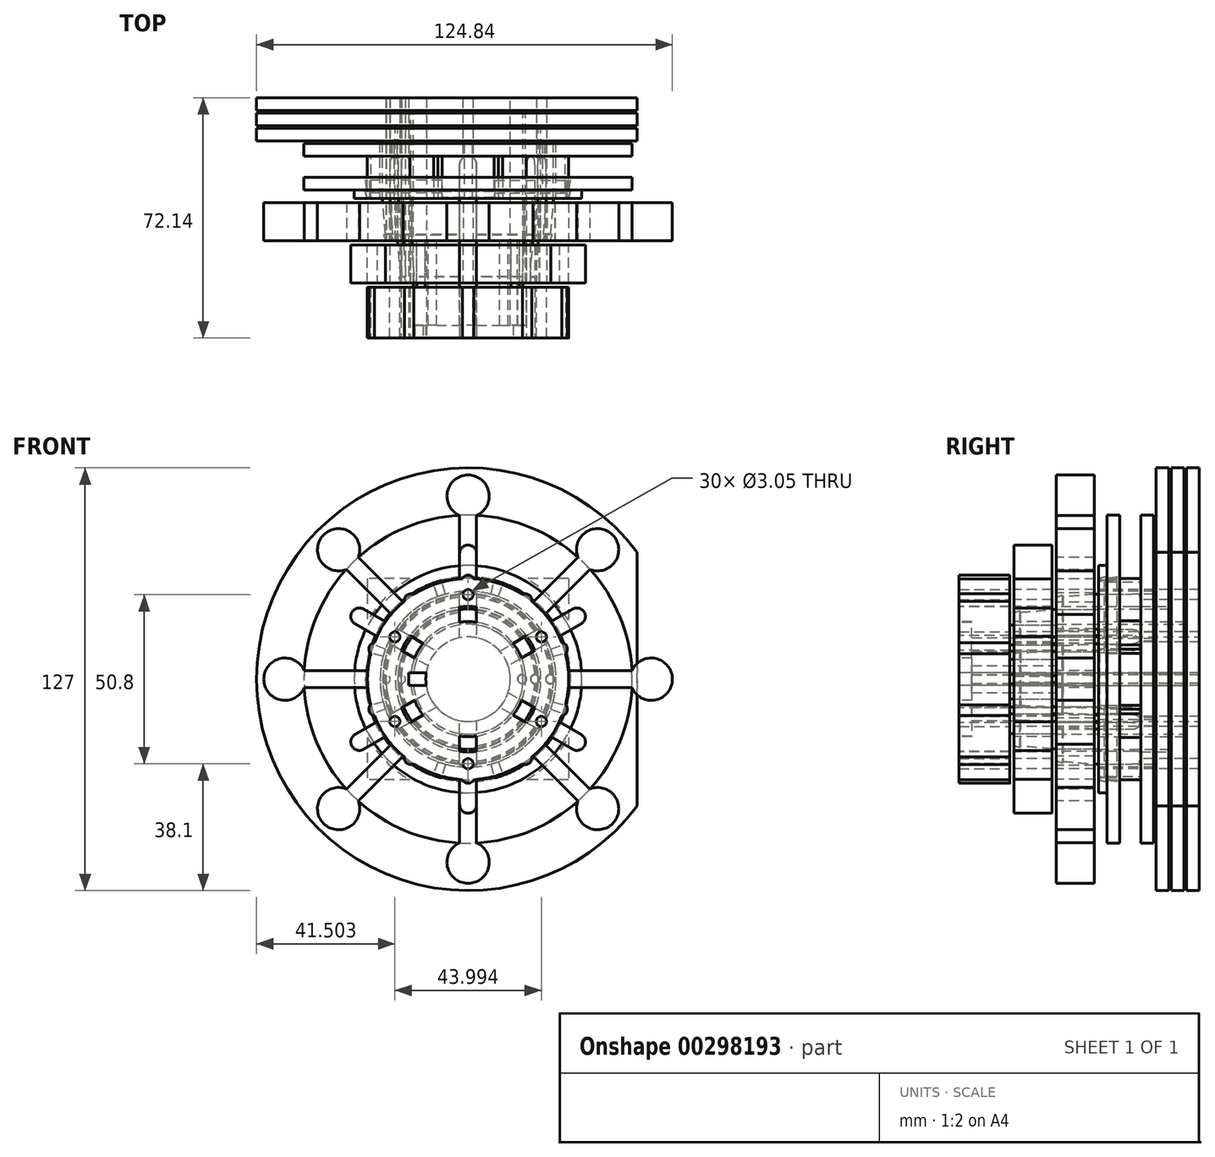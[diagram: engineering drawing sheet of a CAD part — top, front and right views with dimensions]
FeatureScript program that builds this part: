
annotation { "Feature Type Name" : "Feature", "Feature Type Description" : "" }
export const myFeature = defineFeature(function(context is Context, id is Id, definition is map)
    precondition{}
    {
        {
            var Q0;
            Q0=qCreatedBy(makeId("Top.planeOp"),FACE);
            var sketch = newSketch(context, id + "F0", { "sketchPlane" : qUnion([Q0])});
            skLineSegment(sketch, "E0", {"start": v(0, 0) * mm, "end": v(0, -79.23) * mm, "construction": true});
            skLineSegment(sketch, "E1", {"start": v(63.5, 0) * mm, "end": v(12.7, 0) * mm});
            skLineSegment(sketch, "E2", {"start": v(12.7, 0) * mm, "end": v(12.7, -68.33) * mm});
            skLineSegment(sketch, "E3", {"start": v(12.7, -68.33) * mm, "end": v(16.51, -68.33) * mm});
            skLineSegment(sketch, "E4", {"start": v(16.51, -68.33) * mm, "end": v(16.5, -3.81) * mm});
            skLineSegment(sketch, "E5", {"start": v(16.5, -3.81) * mm, "end": v(63.5, -3.8) * mm});
            skLineSegment(sketch, "E6", {"start": v(63.5, -3.8) * mm, "end": v(63.5, 0) * mm});
            skLineSegment(sketch, "E7", {"start": v(63.5, -4.57) * mm, "end": v(17.27, -4.57) * mm});
            skLineSegment(sketch, "E8", {"start": v(17.27, -4.57) * mm, "end": v(17.27, -55.63) * mm});
            skLineSegment(sketch, "E9", {"start": v(17.27, -55.63) * mm, "end": v(21.08, -55.63) * mm});
            skLineSegment(sketch, "E10", {"start": v(21.08, -55.63) * mm, "end": v(21.08, -8.38) * mm});
            skLineSegment(sketch, "E11", {"start": v(21.08, -8.38) * mm, "end": v(63.5, -8.38) * mm});
            skLineSegment(sketch, "E12", {"start": v(63.5, -8.38) * mm, "end": v(63.5, -4.57) * mm});
            skLineSegment(sketch, "E13", {"start": v(63.5, -9.14) * mm, "end": v(21.84, -9.14) * mm});
            skLineSegment(sketch, "E14", {"start": v(21.84, -9.14) * mm, "end": v(21.84, -42.93) * mm});
            skLineSegment(sketch, "E15", {"start": v(21.84, -42.93) * mm, "end": v(25.65, -42.93) * mm});
            skLineSegment(sketch, "E16", {"start": v(25.65, -42.93) * mm, "end": v(25.65, -12.95) * mm});
            skLineSegment(sketch, "E17", {"start": v(25.65, -12.95) * mm, "end": v(63.5, -12.95) * mm});
            skLineSegment(sketch, "E18", {"start": v(63.5, -12.95) * mm, "end": v(63.5, -9.14) * mm});
            skLineSegment(sketch, "E19", {"start": v(49.28, -13.72) * mm, "end": v(26.42, -13.72) * mm});
            skLineSegment(sketch, "E20", {"start": v(26.42, -13.72) * mm, "end": v(26.42, -30.23) * mm});
            skLineSegment(sketch, "E21", {"start": v(26.42, -30.23) * mm, "end": v(30.23, -30.23) * mm});
            skLineSegment(sketch, "E22", {"start": v(30.23, -30.23) * mm, "end": v(30.23, -17.53) * mm});
            skLineSegment(sketch, "E23", {"start": v(30.23, -17.53) * mm, "end": v(49.28, -17.53) * mm});
            skLineSegment(sketch, "E24", {"start": v(49.28, -17.53) * mm, "end": v(49.28, -13.72) * mm});
            skLineSegment(sketch, "E25", {"start": v(49.28, -23.88) * mm, "end": v(30.35, -23.88) * mm});
            skLineSegment(sketch, "E26", {"start": v(30.35, -23.88) * mm, "end": v(30.35, -27.57) * mm});
            skLineSegment(sketch, "E27", {"start": v(30.35, -30.23) * mm, "end": v(34.16, -30.23) * mm});
            skLineSegment(sketch, "E28", {"start": v(34.16, -30.23) * mm, "end": v(34.16, -27.69) * mm});
            skLineSegment(sketch, "E29", {"start": v(34.16, -27.69) * mm, "end": v(49.28, -27.69) * mm});
            skLineSegment(sketch, "E30", {"start": v(49.28, -27.69) * mm, "end": v(49.28, -23.88) * mm});
            skLineSegment(sketch, "E31", {"start": v(25.65, -31.5) * mm, "end": v(24.82, -41.03) * mm});
            skLineSegment(sketch, "E32", {"start": v(21.08, -44.2) * mm, "end": v(20.08, -55.63) * mm});
            skLineSegment(sketch, "E33", {"start": v(16.51, -56.9) * mm, "end": v(15.51, -68.33) * mm});
            skLineSegment(sketch, "E34", {"start": v(25.65, -31.5) * mm, "end": v(30.23, -31.5) * mm});
            skLineSegment(sketch, "E35", {"start": v(30.23, -31.5) * mm, "end": v(30.23, -42.93) * mm});
            skLineSegment(sketch, "E36", {"start": v(30.23, -42.93) * mm, "end": v(25.65, -42.93) * mm});
            skLineSegment(sketch, "E37", {"start": v(21.08, -44.2) * mm, "end": v(30.23, -44.2) * mm});
            skLineSegment(sketch, "E38", {"start": v(30.23, -44.2) * mm, "end": v(30.23, -55.63) * mm});
            skLineSegment(sketch, "E39", {"start": v(30.23, -55.63) * mm, "end": v(21.08, -55.63) * mm});
            skLineSegment(sketch, "E40", {"start": v(16.51, -56.9) * mm, "end": v(30.23, -56.9) * mm});
            skLineSegment(sketch, "E41", {"start": v(30.23, -56.9) * mm, "end": v(30.23, -68.33) * mm});
            skLineSegment(sketch, "E42", {"start": v(30.23, -68.33) * mm, "end": v(16.51, -68.33) * mm});
            skLineSegment(sketch, "E43", {"start": v(25.33, -41.08) * mm, "end": v(24.65, -42.93) * mm});
            skLineSegment(sketch, "E44", {"start": v(25.33, -41.08) * mm, "end": v(24.83, -40.9) * mm});
            skLineSegment(sketch, "E45", {"start": v(25.28, -41.2) * mm, "end": v(24.82, -41.03) * mm});
            skLineSegment(sketch, "E46", {"start": v(30.35, -29.97) * mm, "end": v(30.86, -28.08) * mm});
            skLineSegment(sketch, "E47", {"start": v(30.86, -28.08) * mm, "end": v(30.35, -27.57) * mm});
            skLineSegment(sketch, "E48", {"start": v(30.23, -29.97) * mm, "end": v(30.73, -28.08) * mm});
            skLineSegment(sketch, "E49", {"start": v(30.73, -28.08) * mm, "end": v(30.23, -27.57) * mm});
            skLineSegment(sketch, "E50.trimOffspring", {"start": v(30.35, -29.97) * mm, "end": v(30.35, -30.23) * mm});
            skLineSegment(sketch, "E51", {"start": v(30.35, -27.57) * mm, "end": v(30.86, -23.88) * mm});
            skLineSegment(sketch, "E52", {"start": v(20.08, -55.63) * mm, "end": v(20.73, -53.84) * mm});
            skLineSegment(sketch, "E53", {"start": v(20.73, -53.84) * mm, "end": v(20.25, -53.67) * mm});
            skLineSegment(sketch, "E54", {"start": v(15.51, -68.33) * mm, "end": v(16.16, -66.54) * mm});
            skLineSegment(sketch, "E55", {"start": v(16.16, -66.54) * mm, "end": v(15.68, -66.37) * mm});
            skSolve(sketch);
        }
        {
            var Q0;
            Q0=makeQuery(id+"F0.imprint","IMPRINT",FACE,{"disambiguationData":[TD([[makeQuery(id+"F0.imprint","IMPRINT",EDGE,{"derivedFrom":sQuery(id+"F0.wireOp",EDGE,"E1")}),1.0]])]});
            var Q1;
            Q1=sQuery(id+"F0.wireOp",EDGE,"E0");
            revolve(context, id + "F1", {"entities" : qUnion([Q0]), "axis" : qUnion([Q1]), "revolveType" : RevolveType.FULL});
        }
        {
            var Q0;
            Q0=makeQuery(id+"F0.imprint","IMPRINT",FACE,{"disambiguationData":[TD([[makeQuery(id+"F0.imprint","IMPRINT",EDGE,{"derivedFrom":sQuery(id+"F0.wireOp",EDGE,"E7")}),1.0]])]});
            var Q1;
            {var subQ0=sQuery(id+"F0.wireOp",EDGE,"E52");Q1=makeQuery(id+"F0.imprint","IMPRINT",FACE,{"disambiguationData":[TD([[makeQuery(id+"F0.imprint","IMPRINT",EDGE,{"derivedFrom":subQ0}),1.0]])]});}
            var Q2;
            Q2=sQuery(id+"F0.wireOp",EDGE,"E0");
            revolve(context, id + "F2", {"surfaceOperationType" : NewSurfaceOperationType.NEW, "entities" : qUnion([Q0, Q1]), "axis" : qUnion([Q2]), "revolveType" : RevolveType.FULL});
        }
        {
            var Q0;
            Q0=makeQuery(id+"F0.imprint","IMPRINT",FACE,{"disambiguationData":[TD([[makeQuery(id+"F0.imprint","IMPRINT",EDGE,{"derivedFrom":sQuery(id+"F0.wireOp",EDGE,"E13")}),1.0]])]});
            var Q1;
            Q1=sQuery(id+"F0.wireOp",EDGE,"E0");
            revolve(context, id + "F3", {"entities" : qUnion([Q0]), "axis" : qUnion([Q1]), "revolveType" : RevolveType.FULL});
        }
        {
            var Q0;
            Q0=makeQuery(id+"F0.imprint","IMPRINT",FACE,{"disambiguationData":[TD([[makeQuery(id+"F0.imprint","IMPRINT",EDGE,{"derivedFrom":sQuery(id+"F0.wireOp",EDGE,"E19")}),1.0]])]});
            var Q1;
            {var subQ0=sQuery(id+"F0.wireOp",EDGE,"E48");Q1=makeQuery(id+"F0.imprint","IMPRINT",FACE,{"disambiguationData":[TD([[makeQuery(id+"F0.imprint","IMPRINT",EDGE,{"derivedFrom":subQ0}),1.0]])]});}
            var Q2;
            {var subQ0=sQuery(id+"F0.wireOp",EDGE,"E54");Q2=makeQuery(id+"F0.imprint","IMPRINT",FACE,{"disambiguationData":[TD([[makeQuery(id+"F0.imprint","IMPRINT",EDGE,{"derivedFrom":subQ0}),1.0]])]});}
            var Q3;
            Q3=sQuery(id+"F0.wireOp",EDGE,"E0");
            revolve(context, id + "F4", {"operationType" : NewBodyOperationType.ADD, "surfaceOperationType" : NewSurfaceOperationType.NEW, "entities" : qUnion([Q0, Q1, Q2]), "axis" : qUnion([Q3]), "revolveType" : RevolveType.FULL});
        }
        {
            var Q0;
            Q0=makeQuery(id+"F0.imprint","IMPRINT",FACE,{"disambiguationData":[TD([[makeQuery(id+"F0.imprint","IMPRINT",EDGE,{"derivedFrom":sQuery(id+"F0.wireOp",EDGE,"E27")}),1.0]])]});
            var Q1;
            Q1=sQuery(id+"F0.wireOp",EDGE,"E0");
            revolve(context, id + "F5", {"surfaceOperationType" : NewSurfaceOperationType.NEW, "entities" : qUnion([Q0]), "axis" : qUnion([Q1]), "revolveType" : RevolveType.FULL});
        }
        {
            var Q0;
            Q0=qCreatedBy(makeId("Front.planeOp"),FACE);
            var sketch = newSketch(context, id + "F6", { "sketchPlane" : qUnion([Q0])});
            skCircle(sketch, "E56.0", {"center": v(0, 0) * mm, "radius": 63.5 * mm});
            skLineSegment(sketch, "E57", {"start": v(50.8, 38.1) * mm, "end": v(50.8, -38.1) * mm});
            skSolve(sketch);
        }
        {
            var Q0;
            {var subQ0=sQuery(id+"F6.wireOp",EDGE,"E57");Q0=makeQuery(id+"F6.imprint","IMPRINT",FACE,{"disambiguationData":[TD([[makeQuery(id+"F6.imprint","IMPRINT",EDGE,{"derivedFrom":subQ0}),1.0]])]});}
            extrude(context, id + "F7", {"entities" : qUnion([Q0]), "operationType" : NewBodyOperationType.REMOVE, "endBound" : BoundingType.THROUGH_ALL, "depth" : 25.4 * mm});
        }
        {
            var Q0;
            {var subQ2=sQuery(id+"F0.wireOp",EDGE,"E34");Q0=makeQuery(id+"F0.imprint","IMPRINT",FACE,{"disambiguationData":[TD([[makeQuery(id+"F0.imprint","IMPRINT",EDGE,{"derivedFrom":subQ2}),-1.0]])]});}
            var Q1;
            {var subQ0=sQuery(id+"F0.wireOp",EDGE,"E44");Q1=makeQuery(id+"F0.imprint","IMPRINT",FACE,{"disambiguationData":[TD([[makeQuery(id+"F0.imprint","IMPRINT",EDGE,{"derivedFrom":subQ0}),-1.0]])]});}
            var Q2;
            Q2=sQuery(id+"F0.wireOp",EDGE,"E0");
            revolve(context, id + "F8", {"entities" : qUnion([Q0, Q1]), "axis" : qUnion([Q2]), "revolveType" : RevolveType.FULL});
        }
        {
            var Q0;
            {var subQ2=sQuery(id+"F0.wireOp",EDGE,"E37");Q0=makeQuery(id+"F0.imprint","IMPRINT",FACE,{"disambiguationData":[TD([[makeQuery(id+"F0.imprint","IMPRINT",EDGE,{"derivedFrom":subQ2}),-1.0]])]});}
            var Q1;
            {var subQ0=sQuery(id+"F0.wireOp",EDGE,"E52");Q1=makeQuery(id+"F0.imprint","IMPRINT",FACE,{"disambiguationData":[TD([[makeQuery(id+"F0.imprint","IMPRINT",EDGE,{"derivedFrom":subQ0}),-1.0]])]});}
            var Q2;
            Q2=sQuery(id+"F0.wireOp",EDGE,"E0");
            revolve(context, id + "F9", {"surfaceOperationType" : NewSurfaceOperationType.NEW, "entities" : qUnion([Q0, Q1]), "axis" : qUnion([Q2]), "revolveType" : RevolveType.FULL});
        }
        {
            var Q0;
            {var subQ2=sQuery(id+"F0.wireOp",EDGE,"E40");Q0=makeQuery(id+"F0.imprint","IMPRINT",FACE,{"disambiguationData":[TD([[makeQuery(id+"F0.imprint","IMPRINT",EDGE,{"derivedFrom":subQ2}),-1.0]])]});}
            var Q1;
            {var subQ0=sQuery(id+"F0.wireOp",EDGE,"E54");Q1=makeQuery(id+"F0.imprint","IMPRINT",FACE,{"disambiguationData":[TD([[makeQuery(id+"F0.imprint","IMPRINT",EDGE,{"derivedFrom":subQ0}),-1.0]])]});}
            var Q2;
            Q2=sQuery(id+"F0.wireOp",EDGE,"E0");
            revolve(context, id + "F10", {"surfaceOperationType" : NewSurfaceOperationType.NEW, "entities" : qUnion([Q0, Q1]), "axis" : qUnion([Q2]), "revolveType" : RevolveType.FULL});
        }
        {
            var Q0;
            Q0=makeQuery(id+"F10.opRevolve","SWEPT_FACE",FACE,{"disambiguationData":[OSD([sQuery(id+"F0.wireOp",EDGE,"E3"),sQuery(id+"F0.wireOp",EDGE,"E42")])]});
            var sketch = newSketch(context, id + "F11", { "sketchPlane" : qUnion([Q0])});
            skCircle(sketch, "E58.0", {"center": v(0, 0) * mm, "radius": 30.23 * mm});
            skCircle(sketch, "E59", {"center": v(0, 25.4) * mm, "radius": 1.52 * mm});
            skCircle(sketch, "E60.1.0", {"center": v(-22, 12.7) * mm, "radius": 1.52 * mm});
            skCircle(sketch, "E60.2.0", {"center": v(-22, -12.7) * mm, "radius": 1.52 * mm});
            skCircle(sketch, "E60.3.0", {"center": v(0, -25.4) * mm, "radius": 1.52 * mm});
            skCircle(sketch, "E60.4.0", {"center": v(22, -12.7) * mm, "radius": 1.52 * mm});
            skCircle(sketch, "E60.5.0", {"center": v(22, 12.7) * mm, "radius": 1.52 * mm});
            skSolve(sketch);
        }
        {
            var Q0;
            Q0 = qSketchRegion(id + "F11", true);
            extrude(context, id + "F12", {"entities" : qUnion([Q0]), "operationType" : NewBodyOperationType.ADD, "offsetDistance" : 25.4 * mm, "depth" : 3.8 * mm});
        }
        {
            var Q0;
            Q0=makeQuery(id+"F4.opRevolve","SWEPT_FACE",FACE,{"disambiguationData":[OSD([sQuery(id+"F0.wireOp",EDGE,"E23")])]});
            var sketch = newSketch(context, id + "F13", { "sketchPlane" : qUnion([Q0])});
            skCircle(sketch, "E61.0", {"center": v(0, 0) * mm, "radius": 30.23 * mm});
            skLineSegment(sketch, "E62.bottom", {"start": v(30.23, 30.23) * mm, "end": v(-30.23, 30.23) * mm});
            skLineSegment(sketch, "E62.top", {"start": v(30.23, -30.23) * mm, "end": v(-30.23, -30.23) * mm});
            skLineSegment(sketch, "E62.left", {"start": v(30.23, 30.23) * mm, "end": v(30.23, -30.23) * mm});
            skLineSegment(sketch, "E62.right", {"start": v(-30.23, 30.23) * mm, "end": v(-30.23, -30.23) * mm});
            skCircle(sketch, "E63", {"center": v(0, 0) * mm, "radius": 34.93 * mm});
            skSolve(sketch);
        }
        {
            var Q0;
            Q0=makeQuery(id+"F4.opRevolve","SWEPT_FACE",FACE,{"disambiguationData":[OSD([sQuery(id+"F0.wireOp",EDGE,"E21")])]});
            var sketch = newSketch(context, id + "F14", { "sketchPlane" : qUnion([Q0])});
            skLineSegment(sketch, "E64", {"start": v(0, 0) * mm, "end": v(0, 50.7) * mm, "construction": true});
            skLineSegment(sketch, "E65", {"start": v(0, 0) * mm, "end": v(55.85, 0) * mm, "construction": true});
            skCircle(sketch, "E66", {"center": v(0, 0) * mm, "radius": 30.73 * mm});
            skLineSegment(sketch, "E67", {"start": v(0, 0) * mm, "end": v(-7.95, 29.69) * mm});
            skLineSegment(sketch, "E68.MirrorCS", {"start": v(0, 0) * mm, "end": v(7.95, 29.69) * mm});
            skLineSegment(sketch, "E69", {"start": v(0, 0) * mm, "end": v(29.69, 7.95) * mm});
            skLineSegment(sketch, "E70.MirrorCS", {"start": v(0, 0) * mm, "end": v(29.69, -7.95) * mm});
            skLineSegment(sketch, "E71.MirrorCS", {"start": v(0, 0) * mm, "end": v(-29.69, 7.95) * mm});
            skLineSegment(sketch, "E72.MirrorCS", {"start": v(0, 0) * mm, "end": v(-29.69, -7.95) * mm});
            skLineSegment(sketch, "E73.MirrorCS", {"start": v(0, 0) * mm, "end": v(7.95, -29.69) * mm});
            skLineSegment(sketch, "E74.MirrorCS", {"start": v(0, 0) * mm, "end": v(-7.95, -29.69) * mm});
            skLineSegment(sketch, "E75", {"start": v(0, 0) * mm, "end": v(-10.51, 28.88) * mm});
            skLineSegment(sketch, "E76.MirrorCS", {"start": v(0, 0) * mm, "end": v(10.51, 28.88) * mm});
            skLineSegment(sketch, "E77.MirrorCS", {"start": v(0, 0) * mm, "end": v(10.51, -28.88) * mm});
            skLineSegment(sketch, "E78.MirrorCS", {"start": v(0, 0) * mm, "end": v(-10.51, -28.88) * mm});
            skLineSegment(sketch, "E79", {"start": v(0, 0) * mm, "end": v(28.88, 10.51) * mm});
            skLineSegment(sketch, "E80.MirrorCS", {"start": v(0, 0) * mm, "end": v(28.88, -10.51) * mm});
            skLineSegment(sketch, "E81.MirrorCS", {"start": v(0, 0) * mm, "end": v(-28.88, 10.51) * mm});
            skLineSegment(sketch, "E82.MirrorCS", {"start": v(0, 0) * mm, "end": v(-28.88, -10.51) * mm});
            skSolve(sketch);
        }
        {
            var Q0;
            {var subQ0=sQuery(id+"F13.wireOp",EDGE,"E62.right");var subQ1=sQuery(id+"F13.wireOp",EDGE,"E62.bottom");var subQ2=makeQuery(id+"F13.imprint","INTERSECT",VERTEX,{"derivedFrom":[subQ1,subQ0]});Q0=makeQuery(id+"F13.imprint","IMPRINT",FACE,{"disambiguationData":[TD([[makeQuery(id+"F13.imprint","IMPRINT",EDGE,{"disambiguationData":[TD([[subQ2,1.0]])],"derivedFrom":subQ1}),1.0]])]});}
            var Q1;
            {var subQ0=sQuery(id+"F13.wireOp",EDGE,"E62.left");var subQ1=sQuery(id+"F13.wireOp",EDGE,"E62.bottom");var subQ2=makeQuery(id+"F13.imprint","INTERSECT",VERTEX,{"derivedFrom":[subQ1,subQ0]});Q1=makeQuery(id+"F13.imprint","IMPRINT",FACE,{"disambiguationData":[TD([[makeQuery(id+"F13.imprint","IMPRINT",EDGE,{"disambiguationData":[TD([[subQ2,-1.0]])],"derivedFrom":subQ1}),1.0]])]});}
            var Q2;
            {var subQ0=sQuery(id+"F13.wireOp",EDGE,"E62.left");var subQ1=sQuery(id+"F13.wireOp",EDGE,"E62.top");var subQ2=makeQuery(id+"F13.imprint","INTERSECT",VERTEX,{"derivedFrom":[subQ1,subQ0]});Q2=makeQuery(id+"F13.imprint","IMPRINT",FACE,{"disambiguationData":[TD([[makeQuery(id+"F13.imprint","IMPRINT",EDGE,{"disambiguationData":[TD([[subQ2,-1.0]])],"derivedFrom":subQ1}),-1.0]])]});}
            var Q3;
            {var subQ0=sQuery(id+"F13.wireOp",EDGE,"E62.right");var subQ1=sQuery(id+"F13.wireOp",EDGE,"E62.top");var subQ2=makeQuery(id+"F13.imprint","INTERSECT",VERTEX,{"derivedFrom":[subQ1,subQ0]});Q3=makeQuery(id+"F13.imprint","IMPRINT",FACE,{"disambiguationData":[TD([[makeQuery(id+"F13.imprint","IMPRINT",EDGE,{"disambiguationData":[TD([[subQ2,1.0]])],"derivedFrom":subQ1}),-1.0]])]});}
            var Q4;
            Q4=makeQuery(id+"F4.opRevolve","SWEPT_FACE",FACE,{"disambiguationData":[OSD([sQuery(id+"F0.wireOp",EDGE,"E21")])]});
            extrude(context, id + "F15", {"entities" : qUnion([Q0, Q1, Q2, Q3]), "operationType" : NewBodyOperationType.ADD, "endBoundEntityFace" : qUnion([Q4]), "offsetDistance" : 25.4 * mm, "depth" : 6.35 * mm});
        }
        {
            var Q0;
            Q0=makeQuery(id+"F3.opRevolve","SWEPT_FACE",FACE,{"disambiguationData":[OSD([sQuery(id+"F0.wireOp",EDGE,"E15")])]});
            var sketch = newSketch(context, id + "F16", { "sketchPlane" : qUnion([Q0])});
            skCircle(sketch, "E83", {"center": v(24.65, 0) * mm, "radius": 1.27 * mm});
            skCircle(sketch, "E84", {"center": v(24.65, 0) * mm, "radius": 1.4 * mm});
            skLineSegment(sketch, "E85", {"start": v(0, 0) * mm, "end": v(24.65, 0) * mm, "construction": true});
            skLineSegment(sketch, "E86", {"start": v(0, 0) * mm, "end": v(24.65, 14.23) * mm, "construction": true});
            skLineSegment(sketch, "E87", {"start": v(9.5, 8.42) * mm, "end": v(21.16, 15.15) * mm});
            skLineSegment(sketch, "E88", {"start": v(21.16, 15.15) * mm, "end": v(23.7, 10.75) * mm});
            skLineSegment(sketch, "E89", {"start": v(23.7, 10.75) * mm, "end": v(12.05, 4.02) * mm});
            skLineSegment(sketch, "E90.1.0", {"start": v(2.54, 25.9) * mm, "end": v(2.54, 12.44) * mm});
            skLineSegment(sketch, "E90.1.1", {"start": v(-2.54, 12.44) * mm, "end": v(-2.54, 25.9) * mm});
            skLineSegment(sketch, "E90.1.2", {"start": v(-2.54, 25.9) * mm, "end": v(2.54, 25.9) * mm});
            skLineSegment(sketch, "E90.2.0", {"start": v(-21.16, 15.15) * mm, "end": v(-9.5, 8.42) * mm});
            skLineSegment(sketch, "E90.2.1", {"start": v(-12.05, 4.02) * mm, "end": v(-23.7, 10.75) * mm});
            skLineSegment(sketch, "E90.2.2", {"start": v(-23.7, 10.75) * mm, "end": v(-21.16, 15.15) * mm});
            skLineSegment(sketch, "E90.3.0", {"start": v(-23.7, -10.75) * mm, "end": v(-12.05, -4.02) * mm});
            skLineSegment(sketch, "E90.3.1", {"start": v(-9.5, -8.42) * mm, "end": v(-21.16, -15.15) * mm});
            skLineSegment(sketch, "E90.3.2", {"start": v(-21.16, -15.15) * mm, "end": v(-23.7, -10.75) * mm});
            skPoint(sketch, "E90.center", {"position": v(0, 0) * mm});
            skLineSegment(sketch, "E91.2.4.0", {"start": v(-2.54, -25.9) * mm, "end": v(-2.54, -12.44) * mm});
            skLineSegment(sketch, "E91.3.4.0", {"start": v(2.54, -12.44) * mm, "end": v(2.54, -25.9) * mm});
            skLineSegment(sketch, "E91.6.4.0", {"start": v(2.54, -25.9) * mm, "end": v(-2.54, -25.9) * mm});
            skLineSegment(sketch, "E91.2.5.0", {"start": v(21.16, -15.15) * mm, "end": v(9.5, -8.42) * mm});
            skLineSegment(sketch, "E91.3.5.0", {"start": v(12.05, -4.02) * mm, "end": v(23.7, -10.75) * mm});
            skLineSegment(sketch, "E91.6.5.0", {"start": v(23.7, -10.75) * mm, "end": v(21.16, -15.15) * mm});
            skCircle(sketch, "E92.0", {"center": v(0, 0) * mm, "radius": 17.27 * mm});
            skCircle(sketch, "E93", {"center": v(20.08, 0) * mm, "radius": 1.27 * mm});
            skCircle(sketch, "E94", {"center": v(20.08, 0) * mm, "radius": 1.4 * mm});
            skCircle(sketch, "E95.0", {"center": v(0, 0) * mm, "radius": 12.7 * mm});
            skCircle(sketch, "E96", {"center": v(16.16, 0) * mm, "radius": 1.4 * mm});
            skCircle(sketch, "E97", {"center": v(16.16, 0) * mm, "radius": 1.27 * mm});
            skSolve(sketch);
        }
        {
            var Q0;
            {var subQ0=sQuery(id+"F16.wireOp",EDGE,"E83");var subQ1=makeQuery(id+"F3.opRevolve","SWEPT_EDGE",EDGE,{"disambiguationData":[OSD([sQuery(id+"F0.wireOp",EDGE,"E15"),sQuery(id+"F0.wireOp",EDGE,"E43")])]});var subQ2=makeQuery(id+"F16.imprint","INTERSECT",VERTEX,{"disambiguationData":[OD(0.0)],"derivedFrom":[subQ1,subQ0]});Q0=makeQuery(id+"F16.imprint","IMPRINT",FACE,{"disambiguationData":[TD([[makeQuery(id+"F16.imprint","IMPRINT",EDGE,{"disambiguationData":[TD([[subQ2,1.0]])],"derivedFrom":subQ0}),1.0]])]});}
            var Q1;
            {var subQ0=sQuery(id+"F16.wireOp",EDGE,"E83");var subQ1=makeQuery(id+"F3.opRevolve","SWEPT_EDGE",EDGE,{"disambiguationData":[OSD([sQuery(id+"F0.wireOp",EDGE,"E15"),sQuery(id+"F0.wireOp",EDGE,"E43")])]});var subQ2=makeQuery(id+"F16.imprint","INTERSECT",VERTEX,{"disambiguationData":[OD(0.0)],"derivedFrom":[subQ1,subQ0]});Q1=makeQuery(id+"F16.imprint","IMPRINT",FACE,{"disambiguationData":[TD([[makeQuery(id+"F16.imprint","IMPRINT",EDGE,{"disambiguationData":[TD([[subQ2,-1.0]])],"derivedFrom":subQ0}),1.0]])]});}
            var Q2;
            {var subQ0=sQuery(id+"F16.wireOp",EDGE,"E83");var subQ1=makeQuery(id+"F3.opRevolve","SWEPT_EDGE",EDGE,{"disambiguationData":[OSD([sQuery(id+"F0.wireOp",EDGE,"E15"),sQuery(id+"F0.wireOp",EDGE,"E43")])]});var subQ2=makeQuery(id+"F16.imprint","INTERSECT",VERTEX,{"disambiguationData":[OD(0.0)],"derivedFrom":[subQ1,subQ0]});Q2=makeQuery(id+"F16.imprint","IMPRINT",FACE,{"disambiguationData":[TD([[makeQuery(id+"F16.imprint","IMPRINT",EDGE,{"disambiguationData":[TD([[subQ2,1.0]])],"derivedFrom":subQ0}),-1.0]])]});}
            var Q3;
            {var subQ0=sQuery(id+"F16.wireOp",EDGE,"E83");var subQ1=makeQuery(id+"F3.opRevolve","SWEPT_EDGE",EDGE,{"disambiguationData":[OSD([sQuery(id+"F0.wireOp",EDGE,"E15"),sQuery(id+"F0.wireOp",EDGE,"E43")])]});var subQ2=makeQuery(id+"F16.imprint","INTERSECT",VERTEX,{"disambiguationData":[OD(0.0)],"derivedFrom":[subQ1,subQ0]});Q3=makeQuery(id+"F16.imprint","IMPRINT",FACE,{"disambiguationData":[TD([[makeQuery(id+"F16.imprint","IMPRINT",EDGE,{"disambiguationData":[TD([[subQ2,-1.0]])],"derivedFrom":subQ0}),-1.0]])]});}
            var Q4;
            Q4=makeQuery(id+"F8.opRevolve","SWEPT_FACE",FACE,{"disambiguationData":[OSD([sQuery(id+"F0.wireOp",EDGE,"E34")])]});
            extrude(context, id + "F17", {"entities" : qUnion([Q0, Q1, Q2, Q3]), "operationType" : NewBodyOperationType.REMOVE, "endBound" : BoundingType.UP_TO_SURFACE, "oppositeDirection" : true, "endBoundEntityFace" : qUnion([Q4]), "depth" : 25.4 * mm});
        }
        {
            var Q0;
            {var subQ0=sQuery(id+"F16.wireOp",EDGE,"E83");var subQ1=makeQuery(id+"F3.opRevolve","SWEPT_EDGE",EDGE,{"disambiguationData":[OSD([sQuery(id+"F0.wireOp",EDGE,"E15"),sQuery(id+"F0.wireOp",EDGE,"E43")])]});var subQ2=makeQuery(id+"F16.imprint","INTERSECT",VERTEX,{"disambiguationData":[OD(0.0)],"derivedFrom":[subQ1,subQ0]});Q0=makeQuery(id+"F16.imprint","IMPRINT",FACE,{"disambiguationData":[TD([[makeQuery(id+"F16.imprint","IMPRINT",EDGE,{"disambiguationData":[TD([[subQ2,1.0]])],"derivedFrom":subQ0}),1.0]])]});}
            var Q1;
            {var subQ0=sQuery(id+"F16.wireOp",EDGE,"E83");var subQ1=makeQuery(id+"F3.opRevolve","SWEPT_EDGE",EDGE,{"disambiguationData":[OSD([sQuery(id+"F0.wireOp",EDGE,"E15"),sQuery(id+"F0.wireOp",EDGE,"E43")])]});var subQ2=makeQuery(id+"F16.imprint","INTERSECT",VERTEX,{"disambiguationData":[OD(0.0)],"derivedFrom":[subQ1,subQ0]});Q1=makeQuery(id+"F16.imprint","IMPRINT",FACE,{"disambiguationData":[TD([[makeQuery(id+"F16.imprint","IMPRINT",EDGE,{"disambiguationData":[TD([[subQ2,-1.0]])],"derivedFrom":subQ0}),1.0]])]});}
            var Q2;
            Q2=makeQuery(id+"F8.opRevolve","SWEPT_FACE",FACE,{"disambiguationData":[OSD([sQuery(id+"F0.wireOp",EDGE,"E34")])]});
            extrude(context, id + "F18", {"entities" : qUnion([Q0, Q1]), "operationType" : NewBodyOperationType.ADD, "endBound" : BoundingType.UP_TO_SURFACE, "oppositeDirection" : true, "endBoundEntityFace" : qUnion([Q2]), "depth" : 25.4 * mm});
        }
        {
            var Q0;
            {var subQ0=sQuery(id+"F16.wireOp",EDGE,"E90.1.0");var subQ1=sQuery(id+"F0.wireOp",EDGE,"E15");var subQ2=makeQuery(id+"F3.opRevolve","SWEPT_EDGE",EDGE,{"disambiguationData":[OSD([sQuery(id+"F0.wireOp",EDGE,"E14"),subQ1])]});var subQ3=makeQuery(id+"F16.imprint","INTERSECT",VERTEX,{"derivedFrom":[subQ2,subQ0]});Q0=makeQuery(id+"F16.imprint","IMPRINT",FACE,{"disambiguationData":[TD([[makeQuery(id+"F16.imprint","IMPRINT",EDGE,{"disambiguationData":[TD([[subQ3,1.0]])],"derivedFrom":subQ0}),-1.0]])]});}
            var Q1;
            {var subQ0=sQuery(id+"F16.wireOp",EDGE,"E90.2.0");var subQ1=sQuery(id+"F0.wireOp",EDGE,"E15");var subQ2=makeQuery(id+"F3.opRevolve","SWEPT_EDGE",EDGE,{"disambiguationData":[OSD([sQuery(id+"F0.wireOp",EDGE,"E14"),subQ1])]});var subQ3=makeQuery(id+"F16.imprint","INTERSECT",VERTEX,{"derivedFrom":[subQ2,subQ0]});Q1=makeQuery(id+"F16.imprint","IMPRINT",FACE,{"disambiguationData":[TD([[makeQuery(id+"F16.imprint","IMPRINT",EDGE,{"disambiguationData":[TD([[subQ3,1.0]])],"derivedFrom":subQ0}),-1.0]])]});}
            var Q2;
            {var subQ0=sQuery(id+"F16.wireOp",EDGE,"E87");var subQ1=sQuery(id+"F0.wireOp",EDGE,"E15");var subQ2=makeQuery(id+"F3.opRevolve","SWEPT_EDGE",EDGE,{"disambiguationData":[OSD([sQuery(id+"F0.wireOp",EDGE,"E14"),subQ1])]});var subQ3=makeQuery(id+"F16.imprint","INTERSECT",VERTEX,{"derivedFrom":[subQ2,subQ0]});Q2=makeQuery(id+"F16.imprint","IMPRINT",FACE,{"disambiguationData":[TD([[makeQuery(id+"F16.imprint","IMPRINT",EDGE,{"disambiguationData":[TD([[subQ3,-1.0]])],"derivedFrom":subQ0}),-1.0]])]});}
            var Q3;
            {var subQ0=sQuery(id+"F16.wireOp",EDGE,"E90.3.0");var subQ1=sQuery(id+"F0.wireOp",EDGE,"E15");var subQ2=makeQuery(id+"F3.opRevolve","SWEPT_EDGE",EDGE,{"disambiguationData":[OSD([sQuery(id+"F0.wireOp",EDGE,"E14"),subQ1])]});var subQ3=makeQuery(id+"F16.imprint","INTERSECT",VERTEX,{"derivedFrom":[subQ2,subQ0]});Q3=makeQuery(id+"F16.imprint","IMPRINT",FACE,{"disambiguationData":[TD([[makeQuery(id+"F16.imprint","IMPRINT",EDGE,{"disambiguationData":[TD([[subQ3,1.0]])],"derivedFrom":subQ0}),-1.0]])]});}
            var Q4;
            {var subQ0=sQuery(id+"F16.wireOp",EDGE,"E90.2.2");Q4=makeQuery(id+"F16.imprint","IMPRINT",FACE,{"disambiguationData":[TD([[makeQuery(id+"F16.imprint","IMPRINT",EDGE,{"derivedFrom":subQ0}),-1.0]])]});}
            var Q5;
            {var subQ0=sQuery(id+"F16.wireOp",EDGE,"E90.1.2");Q5=makeQuery(id+"F16.imprint","IMPRINT",FACE,{"disambiguationData":[TD([[makeQuery(id+"F16.imprint","IMPRINT",EDGE,{"derivedFrom":subQ0}),-1.0]])]});}
            var Q6;
            {var subQ0=sQuery(id+"F16.wireOp",EDGE,"E88");Q6=makeQuery(id+"F16.imprint","IMPRINT",FACE,{"disambiguationData":[TD([[makeQuery(id+"F16.imprint","IMPRINT",EDGE,{"derivedFrom":subQ0}),-1.0]])]});}
            var Q7;
            {var subQ0=sQuery(id+"F16.wireOp",EDGE,"E90.3.2");Q7=makeQuery(id+"F16.imprint","IMPRINT",FACE,{"disambiguationData":[TD([[makeQuery(id+"F16.imprint","IMPRINT",EDGE,{"derivedFrom":subQ0}),-1.0]])]});}
            var Q8;
            {var subQ0=sQuery(id+"F16.wireOp",EDGE,"E91.2.4.0");var subQ1=sQuery(id+"F0.wireOp",EDGE,"E15");var subQ2=makeQuery(id+"F3.opRevolve","SWEPT_EDGE",EDGE,{"disambiguationData":[OSD([sQuery(id+"F0.wireOp",EDGE,"E14"),subQ1])]});var subQ3=makeQuery(id+"F16.imprint","INTERSECT",VERTEX,{"derivedFrom":[subQ2,subQ0]});Q8=makeQuery(id+"F16.imprint","IMPRINT",FACE,{"disambiguationData":[TD([[makeQuery(id+"F16.imprint","IMPRINT",EDGE,{"disambiguationData":[TD([[subQ3,1.0]])],"derivedFrom":subQ0}),-1.0]])]});}
            var Q9;
            {var subQ0=sQuery(id+"F16.wireOp",EDGE,"E91.6.4.0");Q9=makeQuery(id+"F16.imprint","IMPRINT",FACE,{"disambiguationData":[TD([[makeQuery(id+"F16.imprint","IMPRINT",EDGE,{"derivedFrom":subQ0}),-1.0]])]});}
            var Q10;
            {var subQ0=sQuery(id+"F16.wireOp",EDGE,"E91.2.5.0");var subQ1=sQuery(id+"F0.wireOp",EDGE,"E15");var subQ2=makeQuery(id+"F3.opRevolve","SWEPT_EDGE",EDGE,{"disambiguationData":[OSD([sQuery(id+"F0.wireOp",EDGE,"E14"),subQ1])]});var subQ3=makeQuery(id+"F16.imprint","INTERSECT",VERTEX,{"derivedFrom":[subQ2,subQ0]});Q10=makeQuery(id+"F16.imprint","IMPRINT",FACE,{"disambiguationData":[TD([[makeQuery(id+"F16.imprint","IMPRINT",EDGE,{"disambiguationData":[TD([[subQ3,1.0]])],"derivedFrom":subQ0}),-1.0]])]});}
            var Q11;
            {var subQ0=sQuery(id+"F16.wireOp",EDGE,"E91.6.5.0");Q11=makeQuery(id+"F16.imprint","IMPRINT",FACE,{"disambiguationData":[TD([[makeQuery(id+"F16.imprint","IMPRINT",EDGE,{"derivedFrom":subQ0}),-1.0]])]});}
            extrude(context, id + "F19", {"entities" : qUnion([Q0, Q1, Q2, Q3, Q4, Q5, Q6, Q7, Q8, Q9, Q10, Q11]), "operationType" : NewBodyOperationType.REMOVE, "oppositeDirection" : true, "depth" : 25.4 * mm});
        }
        {
            var Q0;
            {var subQ0=sQuery(id+"F16.wireOp",EDGE,"E92.0");var subQ1=sQuery(id+"F16.wireOp",EDGE,"E91.2.4.0");var subQ2=makeQuery(id+"F16.imprint","INTERSECT",VERTEX,{"derivedFrom":[subQ1,subQ0]});Q0=makeQuery(id+"F16.imprint","IMPRINT",FACE,{"disambiguationData":[TD([[makeQuery(id+"F16.imprint","IMPRINT",EDGE,{"disambiguationData":[TD([[subQ2,-1.0]])],"derivedFrom":subQ0}),-1.0]])]});}
            var Q1;
            {var subQ0=sQuery(id+"F16.wireOp",EDGE,"E92.0");var subQ1=sQuery(id+"F16.wireOp",EDGE,"E91.2.5.0");var subQ2=makeQuery(id+"F16.imprint","INTERSECT",VERTEX,{"derivedFrom":[subQ1,subQ0]});Q1=makeQuery(id+"F16.imprint","IMPRINT",FACE,{"disambiguationData":[TD([[makeQuery(id+"F16.imprint","IMPRINT",EDGE,{"disambiguationData":[TD([[subQ2,-1.0]])],"derivedFrom":subQ0}),-1.0]])]});}
            var Q2;
            {var subQ0=sQuery(id+"F16.wireOp",EDGE,"E92.0");var subQ1=sQuery(id+"F16.wireOp",EDGE,"E87");var subQ2=makeQuery(id+"F16.imprint","INTERSECT",VERTEX,{"derivedFrom":[subQ1,subQ0]});Q2=makeQuery(id+"F16.imprint","IMPRINT",FACE,{"disambiguationData":[TD([[makeQuery(id+"F16.imprint","IMPRINT",EDGE,{"disambiguationData":[TD([[subQ2,1.0]])],"derivedFrom":subQ0}),-1.0]])]});}
            var Q3;
            {var subQ0=sQuery(id+"F16.wireOp",EDGE,"E92.0");var subQ1=sQuery(id+"F16.wireOp",EDGE,"E90.1.0");var subQ2=makeQuery(id+"F16.imprint","INTERSECT",VERTEX,{"derivedFrom":[subQ1,subQ0]});Q3=makeQuery(id+"F16.imprint","IMPRINT",FACE,{"disambiguationData":[TD([[makeQuery(id+"F16.imprint","IMPRINT",EDGE,{"disambiguationData":[TD([[subQ2,-1.0]])],"derivedFrom":subQ0}),-1.0]])]});}
            var Q4;
            {var subQ0=sQuery(id+"F16.wireOp",EDGE,"E92.0");var subQ1=sQuery(id+"F16.wireOp",EDGE,"E90.2.0");var subQ2=makeQuery(id+"F16.imprint","INTERSECT",VERTEX,{"derivedFrom":[subQ1,subQ0]});Q4=makeQuery(id+"F16.imprint","IMPRINT",FACE,{"disambiguationData":[TD([[makeQuery(id+"F16.imprint","IMPRINT",EDGE,{"disambiguationData":[TD([[subQ2,-1.0]])],"derivedFrom":subQ0}),-1.0]])]});}
            var Q5;
            {var subQ0=sQuery(id+"F16.wireOp",EDGE,"E92.0");var subQ1=sQuery(id+"F16.wireOp",EDGE,"E90.3.0");var subQ2=makeQuery(id+"F16.imprint","INTERSECT",VERTEX,{"derivedFrom":[subQ1,subQ0]});Q5=makeQuery(id+"F16.imprint","IMPRINT",FACE,{"disambiguationData":[TD([[makeQuery(id+"F16.imprint","IMPRINT",EDGE,{"disambiguationData":[TD([[subQ2,-1.0]])],"derivedFrom":subQ0}),-1.0]])]});}
            extrude(context, id + "F20", {"entities" : qUnion([Q0, Q1, Q2, Q3, Q4, Q5]), "operationType" : NewBodyOperationType.REMOVE, "oppositeDirection" : true, "depth" : 12.7 * mm, "offsetDistance" : 25.4 * mm, "hasSecondDirection" : true, "secondDirectionBound" : SecondDirectionBoundingType.THROUGH_ALL, "secondDirectionOppositeDirection" : false, "secondDirectionDepth" : 25.4 * mm});
        }
        {
            var Q0;
            Q0=makeQuery(id+"F16.imprint","IMPRINT",FACE,{"disambiguationData":[TD([[makeQuery(id+"F16.imprint","IMPRINT",EDGE,{"derivedFrom":sQuery(id+"F16.wireOp",EDGE,"E93")}),1.0]])]});
            var Q1;
            Q1=makeQuery(id+"F16.imprint","IMPRINT",FACE,{"disambiguationData":[TD([[makeQuery(id+"F16.imprint","IMPRINT",EDGE,{"derivedFrom":sQuery(id+"F16.wireOp",EDGE,"E93")}),-1.0]])]});
            var Q2;
            Q2=makeQuery(id+"F20.boolean.opBoolean","SPLIT",FACE,{"disambiguationData":[TD([makeQuery(id+"F20.opExtrude","SWEPT_FACE",FACE,{"disambiguationData":[OSD([sQuery(id+"F16.wireOp",EDGE,"E89")])]})])],"derivedFrom":makeQuery(id+"F2.opRevolve","SWEPT_FACE",FACE,{"disambiguationData":[OSD([sQuery(id+"F0.wireOp",EDGE,"E9")])]})});
            extrude(context, id + "F21", {"entities" : qUnion([Q0, Q1]), "operationType" : NewBodyOperationType.REMOVE, "endBound" : BoundingType.UP_TO_SURFACE, "depth" : 25.4 * mm, "endBoundEntityFace" : qUnion([Q2]), "offsetDistance" : 25.4 * mm});
        }
        {
            var Q0;
            Q0=makeQuery(id+"F16.imprint","IMPRINT",FACE,{"disambiguationData":[TD([[makeQuery(id+"F16.imprint","IMPRINT",EDGE,{"derivedFrom":sQuery(id+"F16.wireOp",EDGE,"E93")}),1.0]])]});
            var Q1;
            Q1=makeQuery(id+"F9.opRevolve","SWEPT_FACE",FACE,{"disambiguationData":[OSD([sQuery(id+"F0.wireOp",EDGE,"E9"),sQuery(id+"F0.wireOp",EDGE,"E39")])]});
            var Q2;
            Q2=makeQuery(id+"F9.opRevolve","SWEPT_FACE",FACE,{"disambiguationData":[OSD([sQuery(id+"F0.wireOp",EDGE,"E37")])]});
            extrude(context, id + "F22", {"entities" : qUnion([Q0]), "operationType" : NewBodyOperationType.ADD, "endBound" : BoundingType.UP_TO_SURFACE, "depth" : 25.4 * mm, "endBoundEntityFace" : qUnion([Q1]), "offsetDistance" : 25.4 * mm, "hasSecondDirection" : true, "secondDirectionBound" : SecondDirectionBoundingType.UP_TO_SURFACE, "secondDirectionOppositeDirection" : false, "secondDirectionDepth" : 25.4 * mm, "secondDirectionBoundEntityFace" : qUnion([Q2])});
        }
        {
            var Q0;
            Q0=makeQuery(id+"F19.boolean.opBoolean","COPY",EDGE,{"derivedFrom":makeQuery(id+"F19.opExtrude","CAP_EDGE",EDGE,{"disambiguationData":[OSD([sQuery(id+"F16.wireOp",EDGE,"E90.2.0")])],"isStart":false})});
            var Q1;
            Q1=makeQuery(id+"F19.boolean.opBoolean","COPY",EDGE,{"derivedFrom":makeQuery(id+"F19.opExtrude","CAP_EDGE",EDGE,{"disambiguationData":[OSD([sQuery(id+"F16.wireOp",EDGE,"E90.2.1")])],"isStart":false})});
            var Q2;
            Q2=makeQuery(id+"F19.boolean.opBoolean","COPY",EDGE,{"derivedFrom":makeQuery(id+"F19.opExtrude","CAP_EDGE",EDGE,{"disambiguationData":[OSD([sQuery(id+"F16.wireOp",EDGE,"E90.3.1")])],"isStart":false})});
            var Q3;
            Q3=makeQuery(id+"F19.boolean.opBoolean","COPY",EDGE,{"derivedFrom":makeQuery(id+"F19.opExtrude","CAP_EDGE",EDGE,{"disambiguationData":[OSD([sQuery(id+"F16.wireOp",EDGE,"E90.3.0")])],"isStart":false})});
            var Q4;
            Q4=makeQuery(id+"F19.boolean.opBoolean","COPY",EDGE,{"derivedFrom":makeQuery(id+"F19.opExtrude","CAP_EDGE",EDGE,{"disambiguationData":[OSD([sQuery(id+"F16.wireOp",EDGE,"E89")])],"isStart":false})});
            var Q5;
            Q5=makeQuery(id+"F19.boolean.opBoolean","COPY",EDGE,{"derivedFrom":makeQuery(id+"F19.opExtrude","CAP_EDGE",EDGE,{"disambiguationData":[OSD([sQuery(id+"F16.wireOp",EDGE,"E87")])],"isStart":false})});
            var Q6;
            Q6=makeQuery(id+"F19.boolean.opBoolean","COPY",EDGE,{"derivedFrom":makeQuery(id+"F19.opExtrude","CAP_EDGE",EDGE,{"disambiguationData":[OSD([sQuery(id+"F16.wireOp",EDGE,"E90.1.0")])],"isStart":false})});
            var Q7;
            Q7=makeQuery(id+"F19.boolean.opBoolean","COPY",EDGE,{"derivedFrom":makeQuery(id+"F19.opExtrude","CAP_EDGE",EDGE,{"disambiguationData":[OSD([sQuery(id+"F16.wireOp",EDGE,"E90.1.1")])],"isStart":false})});
            var Q8;
            Q8=makeQuery(id+"F19.boolean.opBoolean","COPY",EDGE,{"derivedFrom":makeQuery(id+"F19.opExtrude","CAP_EDGE",EDGE,{"disambiguationData":[OSD([sQuery(id+"F16.wireOp",EDGE,"E91.3.4.0")])],"isStart":false})});
            var Q9;
            Q9=makeQuery(id+"F19.boolean.opBoolean","COPY",EDGE,{"derivedFrom":makeQuery(id+"F19.opExtrude","CAP_EDGE",EDGE,{"disambiguationData":[OSD([sQuery(id+"F16.wireOp",EDGE,"E91.2.4.0")])],"isStart":false})});
            var Q10;
            Q10=makeQuery(id+"F19.boolean.opBoolean","COPY",EDGE,{"derivedFrom":makeQuery(id+"F19.opExtrude","CAP_EDGE",EDGE,{"disambiguationData":[OSD([sQuery(id+"F16.wireOp",EDGE,"E91.2.5.0")])],"isStart":false})});
            var Q11;
            Q11=makeQuery(id+"F19.boolean.opBoolean","COPY",EDGE,{"derivedFrom":makeQuery(id+"F19.opExtrude","CAP_EDGE",EDGE,{"disambiguationData":[OSD([sQuery(id+"F16.wireOp",EDGE,"E91.3.5.0")])],"isStart":false})});
            fillet(context, id + "F23", {"entities" : qUnion([Q0, Q1, Q2, Q3, Q4, Q5, Q6, Q7, Q8, Q9, Q10, Q11]), "radius" : 2.54 * mm, "tangentPropagation" : true, "allowEdgeOverflow" : false});
        }
        {
            var Q0;
            Q0=makeQuery(id+"F18.boolean.opBoolean","MERGE",FACE,{"derivedFrom":[makeQuery(id+"F8.opRevolve","SWEPT_FACE",FACE,{"disambiguationData":[OSD([sQuery(id+"F0.wireOp",EDGE,"E15"),sQuery(id+"F0.wireOp",EDGE,"E36")])]}),makeQuery(id+"F18.opExtrude","CAP_FACE",FACE,{"disambiguationData":[OSD([sQuery(id+"F16.wireOp",EDGE,"E83")])],"isStart":true})]});
            var sketch = newSketch(context, id + "F24", { "sketchPlane" : qUnion([Q0])});
            skCircle(sketch, "E98.0", {"center": v(0, 0) * mm, "radius": 30.23 * mm});
            skLineSegment(sketch, "E99", {"start": v(0, 0) * mm, "end": v(0, 54.99) * mm, "construction": true});
            skLineSegment(sketch, "E100", {"start": v(2.54, 30.12) * mm, "end": v(2.54, 49.17) * mm});
            skLineSegment(sketch, "E101.MirrorCS", {"start": v(-2.54, 30.12) * mm, "end": v(-2.54, 49.17) * mm});
            skArc(sketch, "E102", {"start": v(2.54, 49.17) * mm, "mid": v(0, 61.34) * mm, "end": v(-2.54, 49.17) * mm});
            skArc(sketch, "E103.1.0", {"start": v(-32.97, 36.56) * mm, "mid": v(-43.37, 43.37) * mm, "end": v(-36.56, 32.97) * mm});
            skLineSegment(sketch, "E103.1.1", {"start": v(0, 0) * mm, "end": v(-38.88, 38.88) * mm, "construction": true});
            skLineSegment(sketch, "E103.1.2", {"start": v(-23.1, 19.5) * mm, "end": v(-36.56, 32.97) * mm});
            skLineSegment(sketch, "E103.1.3", {"start": v(-19.5, 23.1) * mm, "end": v(-32.97, 36.56) * mm});
            skArc(sketch, "E103.2.0", {"start": v(-49.17, 2.54) * mm, "mid": v(-61.34, 0) * mm, "end": v(-49.17, -2.54) * mm});
            skLineSegment(sketch, "E103.2.1", {"start": v(0, 0) * mm, "end": v(-54.99, 0) * mm, "construction": true});
            skLineSegment(sketch, "E103.2.2", {"start": v(-30.12, -2.54) * mm, "end": v(-49.17, -2.54) * mm});
            skLineSegment(sketch, "E103.2.3", {"start": v(-30.12, 2.54) * mm, "end": v(-49.17, 2.54) * mm});
            skArc(sketch, "E103.3.0", {"start": v(-36.56, -32.97) * mm, "mid": v(-43.37, -43.37) * mm, "end": v(-32.97, -36.56) * mm});
            skLineSegment(sketch, "E103.3.1", {"start": v(0, 0) * mm, "end": v(-38.88, -38.88) * mm, "construction": true});
            skLineSegment(sketch, "E103.3.2", {"start": v(-19.5, -23.1) * mm, "end": v(-32.97, -36.56) * mm});
            skLineSegment(sketch, "E103.3.3", {"start": v(-23.1, -19.5) * mm, "end": v(-36.56, -32.97) * mm});
            skArc(sketch, "E103.4.0", {"start": v(-2.54, -49.17) * mm, "mid": v(0, -61.34) * mm, "end": v(2.54, -49.17) * mm});
            skLineSegment(sketch, "E103.4.1", {"start": v(0, 0) * mm, "end": v(0, -54.99) * mm, "construction": true});
            skLineSegment(sketch, "E103.4.2", {"start": v(2.54, -30.12) * mm, "end": v(2.54, -49.17) * mm});
            skLineSegment(sketch, "E103.4.3", {"start": v(-2.54, -30.12) * mm, "end": v(-2.54, -49.17) * mm});
            skArc(sketch, "E103.5.0", {"start": v(32.97, -36.56) * mm, "mid": v(43.37, -43.37) * mm, "end": v(36.56, -32.97) * mm});
            skLineSegment(sketch, "E103.5.1", {"start": v(0, 0) * mm, "end": v(38.88, -38.88) * mm, "construction": true});
            skLineSegment(sketch, "E103.5.2", {"start": v(23.1, -19.5) * mm, "end": v(36.56, -32.97) * mm});
            skLineSegment(sketch, "E103.5.3", {"start": v(19.5, -23.1) * mm, "end": v(32.97, -36.56) * mm});
            skArc(sketch, "E103.6.0", {"start": v(49.17, -2.54) * mm, "mid": v(61.34, 0) * mm, "end": v(49.17, 2.54) * mm});
            skLineSegment(sketch, "E103.6.1", {"start": v(0, 0) * mm, "end": v(54.99, 0) * mm, "construction": true});
            skLineSegment(sketch, "E103.6.2", {"start": v(30.12, 2.54) * mm, "end": v(49.17, 2.54) * mm});
            skLineSegment(sketch, "E103.6.3", {"start": v(30.12, -2.54) * mm, "end": v(49.17, -2.54) * mm});
            skArc(sketch, "E103.7.0", {"start": v(36.56, 32.97) * mm, "mid": v(43.37, 43.37) * mm, "end": v(32.97, 36.56) * mm});
            skLineSegment(sketch, "E103.7.1", {"start": v(0, 0) * mm, "end": v(38.88, 38.88) * mm, "construction": true});
            skLineSegment(sketch, "E103.7.2", {"start": v(19.5, 23.1) * mm, "end": v(32.97, 36.56) * mm});
            skLineSegment(sketch, "E103.7.3", {"start": v(23.1, 19.5) * mm, "end": v(36.56, 32.97) * mm});
            skSolve(sketch);
        }
        {
            var Q0;
            Q0=makeQuery(id+"F24.imprint","IMPRINT",FACE,{"disambiguationData":[TD([[makeQuery(id+"F24.imprint","IMPRINT",EDGE,{"derivedFrom":sQuery(id+"F24.wireOp",EDGE,"E103.1.0")}),1.0]])]});
            var Q1;
            {var subQ0=sQuery(id+"F24.wireOp",EDGE,"E100");Q1=makeQuery(id+"F24.imprint","IMPRINT",FACE,{"disambiguationData":[TD([[makeQuery(id+"F24.imprint","IMPRINT",EDGE,{"derivedFrom":subQ0}),1.0]])]});}
            var Q2;
            Q2=makeQuery(id+"F24.imprint","IMPRINT",FACE,{"disambiguationData":[TD([[makeQuery(id+"F24.imprint","IMPRINT",EDGE,{"derivedFrom":sQuery(id+"F24.wireOp",EDGE,"E103.7.0")}),1.0]])]});
            var Q3;
            Q3=makeQuery(id+"F24.imprint","IMPRINT",FACE,{"disambiguationData":[TD([[makeQuery(id+"F24.imprint","IMPRINT",EDGE,{"derivedFrom":sQuery(id+"F24.wireOp",EDGE,"E103.6.0")}),1.0]])]});
            var Q4;
            Q4=makeQuery(id+"F24.imprint","IMPRINT",FACE,{"disambiguationData":[TD([[makeQuery(id+"F24.imprint","IMPRINT",EDGE,{"derivedFrom":sQuery(id+"F24.wireOp",EDGE,"E103.5.0")}),1.0]])]});
            var Q5;
            Q5=makeQuery(id+"F24.imprint","IMPRINT",FACE,{"disambiguationData":[TD([[makeQuery(id+"F24.imprint","IMPRINT",EDGE,{"derivedFrom":sQuery(id+"F24.wireOp",EDGE,"E103.4.0")}),1.0]])]});
            var Q6;
            Q6=makeQuery(id+"F24.imprint","IMPRINT",FACE,{"disambiguationData":[TD([[makeQuery(id+"F24.imprint","IMPRINT",EDGE,{"derivedFrom":sQuery(id+"F24.wireOp",EDGE,"E103.3.0")}),1.0]])]});
            var Q7;
            Q7=makeQuery(id+"F24.imprint","IMPRINT",FACE,{"disambiguationData":[TD([[makeQuery(id+"F24.imprint","IMPRINT",EDGE,{"derivedFrom":sQuery(id+"F24.wireOp",EDGE,"E103.2.0")}),1.0]])]});
            var Q8;
            {var subQ0=sQuery(id+"F0.wireOp",EDGE,"E34");Q8=makeQuery(id+"F18.boolean.opBoolean","MERGE",FACE,{"derivedFrom":[makeQuery(id+"F8.opRevolve","SWEPT_FACE",FACE,{"disambiguationData":[OSD([subQ0])]}),makeQuery(id+"F18.opExtrude","CAP_FACE",FACE,{"disambiguationData":[OSD([subQ0])],"isStart":false})]});}
            extrude(context, id + "F25", {"entities" : qUnion([Q0, Q1, Q2, Q3, Q4, Q5, Q6, Q7]), "operationType" : NewBodyOperationType.ADD, "endBound" : BoundingType.UP_TO_SURFACE, "oppositeDirection" : true, "endBoundEntityFace" : qUnion([Q8]), "depth" : 25.4 * mm});
        }
        {
            var Q0;
            Q0=makeQuery(id+"F9.opRevolve","SWEPT_FACE",FACE,{"disambiguationData":[OSD([sQuery(id+"F0.wireOp",EDGE,"E9"),sQuery(id+"F0.wireOp",EDGE,"E39")])]});
            var sketch = newSketch(context, id + "F26", { "sketchPlane" : qUnion([Q0])});
            skCircle(sketch, "E104.0", {"center": v(0, 0) * mm, "radius": 30.23 * mm});
            skLineSegment(sketch, "E105", {"start": v(0, 0) * mm, "end": v(0, 47.16) * mm, "construction": true});
            skLineSegment(sketch, "E106", {"start": v(-2.54, 30.12) * mm, "end": v(-2.54, 37.74) * mm});
            skLineSegment(sketch, "E107.MirrorCS", {"start": v(2.54, 30.12) * mm, "end": v(2.54, 37.74) * mm});
            skArc(sketch, "E108", {"start": v(2.54, 37.74) * mm, "mid": v(0, 40.28) * mm, "end": v(-2.54, 37.74) * mm});
            skLineSegment(sketch, "E109.1.0", {"start": v(-27.35, 12.86) * mm, "end": v(-33.95, 16.67) * mm});
            skArc(sketch, "E109.1.1", {"start": v(-31.41, 21.07) * mm, "mid": v(-34.88, 20.14) * mm, "end": v(-33.95, 16.67) * mm});
            skLineSegment(sketch, "E109.1.2", {"start": v(-24.81, 17.26) * mm, "end": v(-31.41, 21.07) * mm});
            skLineSegment(sketch, "E109.1.3", {"start": v(0, 0) * mm, "end": v(-40.84, 23.58) * mm, "construction": true});
            skLineSegment(sketch, "E109.2.0", {"start": v(-24.81, -17.26) * mm, "end": v(-31.41, -21.07) * mm});
            skArc(sketch, "E109.2.1", {"start": v(-33.95, -16.67) * mm, "mid": v(-34.88, -20.14) * mm, "end": v(-31.41, -21.07) * mm});
            skLineSegment(sketch, "E109.2.2", {"start": v(-27.35, -12.86) * mm, "end": v(-33.95, -16.67) * mm});
            skLineSegment(sketch, "E109.2.3", {"start": v(0, 0) * mm, "end": v(-40.84, -23.58) * mm, "construction": true});
            skLineSegment(sketch, "E109.3.0", {"start": v(2.54, -30.12) * mm, "end": v(2.54, -37.74) * mm});
            skArc(sketch, "E109.3.1", {"start": v(-2.54, -37.74) * mm, "mid": v(0, -40.28) * mm, "end": v(2.54, -37.74) * mm});
            skLineSegment(sketch, "E109.3.2", {"start": v(-2.54, -30.12) * mm, "end": v(-2.54, -37.74) * mm});
            skLineSegment(sketch, "E109.3.3", {"start": v(0, 0) * mm, "end": v(0, -47.16) * mm, "construction": true});
            skLineSegment(sketch, "E109.4.0", {"start": v(27.35, -12.86) * mm, "end": v(33.95, -16.67) * mm});
            skArc(sketch, "E109.4.1", {"start": v(31.41, -21.07) * mm, "mid": v(34.88, -20.14) * mm, "end": v(33.95, -16.67) * mm});
            skLineSegment(sketch, "E109.4.2", {"start": v(24.81, -17.26) * mm, "end": v(31.41, -21.07) * mm});
            skLineSegment(sketch, "E109.4.3", {"start": v(0, 0) * mm, "end": v(40.84, -23.58) * mm, "construction": true});
            skLineSegment(sketch, "E109.5.0", {"start": v(24.81, 17.26) * mm, "end": v(31.41, 21.07) * mm});
            skArc(sketch, "E109.5.1", {"start": v(33.95, 16.67) * mm, "mid": v(34.88, 20.14) * mm, "end": v(31.41, 21.07) * mm});
            skLineSegment(sketch, "E109.5.2", {"start": v(27.35, 12.86) * mm, "end": v(33.95, 16.67) * mm});
            skLineSegment(sketch, "E109.5.3", {"start": v(0, 0) * mm, "end": v(40.84, 23.58) * mm, "construction": true});
            skSolve(sketch);
        }
        {
            var Q0;
            {var subQ0=sQuery(id+"F26.wireOp",EDGE,"E106");Q0=makeQuery(id+"F26.imprint","IMPRINT",FACE,{"disambiguationData":[TD([[makeQuery(id+"F26.imprint","IMPRINT",EDGE,{"derivedFrom":subQ0}),-1.0]])]});}
            var Q1;
            {var subQ0=sQuery(id+"F26.wireOp",EDGE,"E109.1.0");Q1=makeQuery(id+"F26.imprint","IMPRINT",FACE,{"disambiguationData":[TD([[makeQuery(id+"F26.imprint","IMPRINT",EDGE,{"derivedFrom":subQ0}),-1.0]])]});}
            var Q2;
            {var subQ0=sQuery(id+"F26.wireOp",EDGE,"E109.2.0");Q2=makeQuery(id+"F26.imprint","IMPRINT",FACE,{"disambiguationData":[TD([[makeQuery(id+"F26.imprint","IMPRINT",EDGE,{"derivedFrom":subQ0}),-1.0]])]});}
            var Q3;
            {var subQ0=sQuery(id+"F26.wireOp",EDGE,"E109.3.0");Q3=makeQuery(id+"F26.imprint","IMPRINT",FACE,{"disambiguationData":[TD([[makeQuery(id+"F26.imprint","IMPRINT",EDGE,{"derivedFrom":subQ0}),-1.0]])]});}
            var Q4;
            {var subQ0=sQuery(id+"F26.wireOp",EDGE,"E109.4.0");Q4=makeQuery(id+"F26.imprint","IMPRINT",FACE,{"disambiguationData":[TD([[makeQuery(id+"F26.imprint","IMPRINT",EDGE,{"derivedFrom":subQ0}),-1.0]])]});}
            var Q5;
            {var subQ0=sQuery(id+"F26.wireOp",EDGE,"E109.5.0");Q5=makeQuery(id+"F26.imprint","IMPRINT",FACE,{"disambiguationData":[TD([[makeQuery(id+"F26.imprint","IMPRINT",EDGE,{"derivedFrom":subQ0}),-1.0]])]});}
            var Q6;
            Q6=makeQuery(id+"F9.opRevolve","SWEPT_FACE",FACE,{"disambiguationData":[OSD([sQuery(id+"F0.wireOp",EDGE,"E37")])]});
            extrude(context, id + "F27", {"entities" : qUnion([Q0, Q1, Q2, Q3, Q4, Q5]), "operationType" : NewBodyOperationType.ADD, "endBound" : BoundingType.UP_TO_SURFACE, "oppositeDirection" : true, "endBoundEntityFace" : qUnion([Q6]), "depth" : 25.4 * mm});
        }
        {
            var Q0;
            Q0=makeQuery(id+"F12.opExtrude","CAP_FACE",FACE,{"disambiguationData":[OSD([sQuery(id+"F11.wireOp",EDGE,"E58.0"),sQuery(id+"F11.wireOp",EDGE,"E59"),sQuery(id+"F11.wireOp",EDGE,"E60.1.0"),sQuery(id+"F11.wireOp",EDGE,"E60.2.0"),sQuery(id+"F11.wireOp",EDGE,"E60.3.0"),sQuery(id+"F11.wireOp",EDGE,"E60.4.0"),sQuery(id+"F11.wireOp",EDGE,"E60.5.0")])],"isStart":false});
            var sketch = newSketch(context, id + "F28", { "sketchPlane" : qUnion([Q0])});
            skCircle(sketch, "E110.0.0", {"center": v(0, 0) * mm, "radius": 30.23 * mm});
            skLineSegment(sketch, "E111", {"start": v(0, 0) * mm, "end": v(0, 29.9) * mm, "construction": true});
            skCircle(sketch, "E112", {"center": v(0, 29.34) * mm, "radius": 1.9 * mm});
            skLineSegment(sketch, "E113.1.0", {"start": v(0, 0) * mm, "end": v(-17.58, 24.2) * mm, "construction": true});
            skCircle(sketch, "E113.1.1", {"center": v(-17.24, 23.73) * mm, "radius": 1.9 * mm});
            skLineSegment(sketch, "E113.2.0", {"start": v(0, 0) * mm, "end": v(-28.44, 9.24) * mm, "construction": true});
            skCircle(sketch, "E113.2.1", {"center": v(-27.9, 9.07) * mm, "radius": 1.9 * mm});
            skLineSegment(sketch, "E113.3.0", {"start": v(0, 0) * mm, "end": v(-28.44, -9.24) * mm, "construction": true});
            skCircle(sketch, "E113.3.1", {"center": v(-27.9, -9.07) * mm, "radius": 1.9 * mm});
            skLineSegment(sketch, "E113.4.0", {"start": v(0, 0) * mm, "end": v(-17.58, -24.2) * mm, "construction": true});
            skCircle(sketch, "E113.4.1", {"center": v(-17.24, -23.73) * mm, "radius": 1.9 * mm});
            skLineSegment(sketch, "E113.5.0", {"start": v(0, 0) * mm, "end": v(0, -29.9) * mm, "construction": true});
            skCircle(sketch, "E113.5.1", {"center": v(0, -29.34) * mm, "radius": 1.9 * mm});
            skLineSegment(sketch, "E113.6.0", {"start": v(0, 0) * mm, "end": v(17.58, -24.2) * mm, "construction": true});
            skCircle(sketch, "E113.6.1", {"center": v(17.24, -23.73) * mm, "radius": 1.9 * mm});
            skLineSegment(sketch, "E113.7.0", {"start": v(0, 0) * mm, "end": v(28.44, -9.24) * mm, "construction": true});
            skCircle(sketch, "E113.7.1", {"center": v(27.9, -9.07) * mm, "radius": 1.9 * mm});
            skLineSegment(sketch, "E113.8.0", {"start": v(0, 0) * mm, "end": v(28.44, 9.24) * mm, "construction": true});
            skCircle(sketch, "E113.8.1", {"center": v(27.9, 9.07) * mm, "radius": 1.9 * mm});
            skLineSegment(sketch, "E113.9.0", {"start": v(0, 0) * mm, "end": v(17.58, 24.2) * mm, "construction": true});
            skCircle(sketch, "E113.9.1", {"center": v(17.24, 23.73) * mm, "radius": 1.9 * mm});
            skSolve(sketch);
        }
        {
            var Q0;
            {var subQ0=sQuery(id+"F28.wireOp",EDGE,"E112");var subQ1=sQuery(id+"F28.wireOp",EDGE,"E110.0.0");var subQ2=makeQuery(id+"F28.imprint","INTERSECT",VERTEX,{"disambiguationData":[OD(0.0)],"derivedFrom":[subQ1,subQ0]});Q0=makeQuery(id+"F28.imprint","IMPRINT",FACE,{"disambiguationData":[TD([[makeQuery(id+"F28.imprint","IMPRINT",EDGE,{"disambiguationData":[TD([[subQ2,1.0]])],"derivedFrom":subQ1}),1.0]])]});}
            var Q1;
            {var subQ0=sQuery(id+"F28.wireOp",EDGE,"E113.1.1");var subQ1=sQuery(id+"F28.wireOp",EDGE,"E110.0.0");var subQ2=makeQuery(id+"F28.imprint","INTERSECT",VERTEX,{"disambiguationData":[OD(0.0)],"derivedFrom":[subQ1,subQ0]});Q1=makeQuery(id+"F28.imprint","IMPRINT",FACE,{"disambiguationData":[TD([[makeQuery(id+"F28.imprint","IMPRINT",EDGE,{"disambiguationData":[TD([[subQ2,-1.0]])],"derivedFrom":subQ1}),1.0]])]});}
            var Q2;
            {var subQ0=sQuery(id+"F28.wireOp",EDGE,"E113.2.1");var subQ1=sQuery(id+"F28.wireOp",EDGE,"E110.0.0");var subQ2=makeQuery(id+"F28.imprint","INTERSECT",VERTEX,{"disambiguationData":[OD(0.0)],"derivedFrom":[subQ1,subQ0]});Q2=makeQuery(id+"F28.imprint","IMPRINT",FACE,{"disambiguationData":[TD([[makeQuery(id+"F28.imprint","IMPRINT",EDGE,{"disambiguationData":[TD([[subQ2,-1.0]])],"derivedFrom":subQ1}),1.0]])]});}
            var Q3;
            {var subQ0=sQuery(id+"F28.wireOp",EDGE,"E113.3.1");var subQ1=sQuery(id+"F28.wireOp",EDGE,"E110.0.0");var subQ2=makeQuery(id+"F28.imprint","INTERSECT",VERTEX,{"disambiguationData":[OD(0.0)],"derivedFrom":[subQ1,subQ0]});Q3=makeQuery(id+"F28.imprint","IMPRINT",FACE,{"disambiguationData":[TD([[makeQuery(id+"F28.imprint","IMPRINT",EDGE,{"disambiguationData":[TD([[subQ2,-1.0]])],"derivedFrom":subQ1}),1.0]])]});}
            var Q4;
            {var subQ0=sQuery(id+"F28.wireOp",EDGE,"E113.4.1");var subQ1=sQuery(id+"F28.wireOp",EDGE,"E110.0.0");var subQ2=makeQuery(id+"F28.imprint","INTERSECT",VERTEX,{"disambiguationData":[OD(0.0)],"derivedFrom":[subQ1,subQ0]});Q4=makeQuery(id+"F28.imprint","IMPRINT",FACE,{"disambiguationData":[TD([[makeQuery(id+"F28.imprint","IMPRINT",EDGE,{"disambiguationData":[TD([[subQ2,-1.0]])],"derivedFrom":subQ1}),1.0]])]});}
            var Q5;
            {var subQ0=sQuery(id+"F28.wireOp",EDGE,"E113.5.1");var subQ1=sQuery(id+"F28.wireOp",EDGE,"E110.0.0");var subQ2=makeQuery(id+"F28.imprint","INTERSECT",VERTEX,{"disambiguationData":[OD(0.0)],"derivedFrom":[subQ1,subQ0]});Q5=makeQuery(id+"F28.imprint","IMPRINT",FACE,{"disambiguationData":[TD([[makeQuery(id+"F28.imprint","IMPRINT",EDGE,{"disambiguationData":[TD([[subQ2,-1.0]])],"derivedFrom":subQ1}),1.0]])]});}
            var Q6;
            {var subQ0=sQuery(id+"F28.wireOp",EDGE,"E113.6.1");var subQ1=sQuery(id+"F28.wireOp",EDGE,"E110.0.0");var subQ2=makeQuery(id+"F28.imprint","INTERSECT",VERTEX,{"disambiguationData":[OD(0.0)],"derivedFrom":[subQ1,subQ0]});Q6=makeQuery(id+"F28.imprint","IMPRINT",FACE,{"disambiguationData":[TD([[makeQuery(id+"F28.imprint","IMPRINT",EDGE,{"disambiguationData":[TD([[subQ2,-1.0]])],"derivedFrom":subQ1}),1.0]])]});}
            var Q7;
            {var subQ0=sQuery(id+"F28.wireOp",EDGE,"E113.7.1");var subQ1=sQuery(id+"F28.wireOp",EDGE,"E110.0.0");var subQ2=makeQuery(id+"F28.imprint","INTERSECT",VERTEX,{"disambiguationData":[OD(0.0)],"derivedFrom":[subQ1,subQ0]});Q7=makeQuery(id+"F28.imprint","IMPRINT",FACE,{"disambiguationData":[TD([[makeQuery(id+"F28.imprint","IMPRINT",EDGE,{"disambiguationData":[TD([[subQ2,-1.0]])],"derivedFrom":subQ1}),1.0]])]});}
            var Q8;
            {var subQ0=sQuery(id+"F28.wireOp",EDGE,"E113.8.1");var subQ1=sQuery(id+"F28.wireOp",EDGE,"E110.0.0");var subQ2=makeQuery(id+"F28.imprint","INTERSECT",VERTEX,{"disambiguationData":[OD(0.0)],"derivedFrom":[subQ1,subQ0]});Q8=makeQuery(id+"F28.imprint","IMPRINT",FACE,{"disambiguationData":[TD([[makeQuery(id+"F28.imprint","IMPRINT",EDGE,{"disambiguationData":[TD([[subQ2,-1.0]])],"derivedFrom":subQ1}),1.0]])]});}
            var Q9;
            {var subQ0=sQuery(id+"F28.wireOp",EDGE,"E113.9.1");var subQ1=sQuery(id+"F28.wireOp",EDGE,"E110.0.0");var subQ2=makeQuery(id+"F28.imprint","INTERSECT",VERTEX,{"disambiguationData":[OD(0.0)],"derivedFrom":[subQ1,subQ0]});Q9=makeQuery(id+"F28.imprint","IMPRINT",FACE,{"disambiguationData":[TD([[makeQuery(id+"F28.imprint","IMPRINT",EDGE,{"disambiguationData":[TD([[subQ2,-1.0]])],"derivedFrom":subQ1}),1.0]])]});}
            var Q10;
            Q10=makeQuery(id+"F10.opRevolve","SWEPT_FACE",FACE,{"disambiguationData":[OSD([sQuery(id+"F0.wireOp",EDGE,"E40")])]});
            extrude(context, id + "F29", {"entities" : qUnion([Q0, Q1, Q2, Q3, Q4, Q5, Q6, Q7, Q8, Q9]), "operationType" : NewBodyOperationType.ADD, "endBound" : BoundingType.UP_TO_SURFACE, "oppositeDirection" : true, "endBoundEntityFace" : qUnion([Q10]), "depth" : 25.4 * mm});
        }
        {
            var Q0;
            {var subQ0=sQuery(id+"F14.wireOp",EDGE,"E68.MirrorCS");var subQ1=sQuery(id+"F14.wireOp",EDGE,"E66");var subQ2=makeQuery(id+"F14.imprint","INTERSECT",VERTEX,{"derivedFrom":[subQ1,subQ0]});Q0=makeQuery(id+"F14.imprint","IMPRINT",FACE,{"disambiguationData":[TD([[makeQuery(id+"F14.imprint","IMPRINT",EDGE,{"disambiguationData":[TD([[subQ2,1.0]])],"derivedFrom":subQ1}),1.0]])]});}
            var Q1;
            {var subQ0=sQuery(id+"F14.wireOp",EDGE,"E68.MirrorCS");var subQ1=sQuery(id+"F0.wireOp",EDGE,"E21");var subQ2=makeQuery(id+"F4.opRevolve","SWEPT_EDGE",EDGE,{"disambiguationData":[OSD([sQuery(id+"F0.wireOp",EDGE,"E20"),subQ1])]});var subQ3=makeQuery(id+"F14.imprint","INTERSECT",VERTEX,{"derivedFrom":[subQ2,subQ0]});Q1=makeQuery(id+"F14.imprint","IMPRINT",FACE,{"disambiguationData":[TD([[makeQuery(id+"F14.imprint","IMPRINT",EDGE,{"disambiguationData":[TD([[subQ3,-1.0]])],"derivedFrom":subQ0}),-1.0]])]});}
            var Q2;
            {var subQ0=sQuery(id+"F14.wireOp",EDGE,"E76.MirrorCS");var subQ1=sQuery(id+"F14.wireOp",EDGE,"E66");var subQ2=makeQuery(id+"F14.imprint","INTERSECT",VERTEX,{"derivedFrom":[subQ1,subQ0]});Q2=makeQuery(id+"F14.imprint","IMPRINT",FACE,{"disambiguationData":[TD([[makeQuery(id+"F14.imprint","IMPRINT",EDGE,{"disambiguationData":[TD([[subQ2,1.0]])],"derivedFrom":subQ1}),1.0]])]});}
            var Q3;
            {var subQ0=sQuery(id+"F14.wireOp",EDGE,"E69");var subQ1=sQuery(id+"F14.wireOp",EDGE,"E66");var subQ2=makeQuery(id+"F14.imprint","INTERSECT",VERTEX,{"derivedFrom":[subQ1,subQ0]});Q3=makeQuery(id+"F14.imprint","IMPRINT",FACE,{"disambiguationData":[TD([[makeQuery(id+"F14.imprint","IMPRINT",EDGE,{"disambiguationData":[TD([[subQ2,-1.0]])],"derivedFrom":subQ1}),1.0]])]});}
            var Q4;
            {var subQ0=sQuery(id+"F14.wireOp",EDGE,"E69");var subQ1=sQuery(id+"F0.wireOp",EDGE,"E21");var subQ2=makeQuery(id+"F4.opRevolve","SWEPT_EDGE",EDGE,{"disambiguationData":[OSD([sQuery(id+"F0.wireOp",EDGE,"E20"),subQ1])]});var subQ3=makeQuery(id+"F14.imprint","INTERSECT",VERTEX,{"derivedFrom":[subQ2,subQ0]});Q4=makeQuery(id+"F14.imprint","IMPRINT",FACE,{"disambiguationData":[TD([[makeQuery(id+"F14.imprint","IMPRINT",EDGE,{"disambiguationData":[TD([[subQ3,-1.0]])],"derivedFrom":subQ0}),1.0]])]});}
            var Q5;
            {var subQ0=sQuery(id+"F14.wireOp",EDGE,"E70.MirrorCS");var subQ1=sQuery(id+"F14.wireOp",EDGE,"E66");var subQ2=makeQuery(id+"F14.imprint","INTERSECT",VERTEX,{"derivedFrom":[subQ1,subQ0]});Q5=makeQuery(id+"F14.imprint","IMPRINT",FACE,{"disambiguationData":[TD([[makeQuery(id+"F14.imprint","IMPRINT",EDGE,{"disambiguationData":[TD([[subQ2,1.0]])],"derivedFrom":subQ1}),1.0]])]});}
            var Q6;
            {var subQ0=sQuery(id+"F14.wireOp",EDGE,"E70.MirrorCS");var subQ1=sQuery(id+"F0.wireOp",EDGE,"E21");var subQ2=makeQuery(id+"F4.opRevolve","SWEPT_EDGE",EDGE,{"disambiguationData":[OSD([sQuery(id+"F0.wireOp",EDGE,"E20"),subQ1])]});var subQ3=makeQuery(id+"F14.imprint","INTERSECT",VERTEX,{"derivedFrom":[subQ2,subQ0]});Q6=makeQuery(id+"F14.imprint","IMPRINT",FACE,{"disambiguationData":[TD([[makeQuery(id+"F14.imprint","IMPRINT",EDGE,{"disambiguationData":[TD([[subQ3,-1.0]])],"derivedFrom":subQ0}),-1.0]])]});}
            var Q7;
            {var subQ0=sQuery(id+"F14.wireOp",EDGE,"E67");var subQ1=sQuery(id+"F14.wireOp",EDGE,"E66");var subQ2=makeQuery(id+"F14.imprint","INTERSECT",VERTEX,{"derivedFrom":[subQ1,subQ0]});Q7=makeQuery(id+"F14.imprint","IMPRINT",FACE,{"disambiguationData":[TD([[makeQuery(id+"F14.imprint","IMPRINT",EDGE,{"disambiguationData":[TD([[subQ2,-1.0]])],"derivedFrom":subQ1}),1.0]])]});}
            var Q8;
            {var subQ0=sQuery(id+"F14.wireOp",EDGE,"E67");var subQ1=sQuery(id+"F0.wireOp",EDGE,"E21");var subQ2=makeQuery(id+"F4.opRevolve","SWEPT_EDGE",EDGE,{"disambiguationData":[OSD([sQuery(id+"F0.wireOp",EDGE,"E20"),subQ1])]});var subQ3=makeQuery(id+"F14.imprint","INTERSECT",VERTEX,{"derivedFrom":[subQ2,subQ0]});Q8=makeQuery(id+"F14.imprint","IMPRINT",FACE,{"disambiguationData":[TD([[makeQuery(id+"F14.imprint","IMPRINT",EDGE,{"disambiguationData":[TD([[subQ3,-1.0]])],"derivedFrom":subQ0}),1.0]])]});}
            var Q9;
            {var subQ0=sQuery(id+"F14.wireOp",EDGE,"E75");var subQ1=sQuery(id+"F14.wireOp",EDGE,"E66");var subQ2=makeQuery(id+"F14.imprint","INTERSECT",VERTEX,{"derivedFrom":[subQ1,subQ0]});Q9=makeQuery(id+"F14.imprint","IMPRINT",FACE,{"disambiguationData":[TD([[makeQuery(id+"F14.imprint","IMPRINT",EDGE,{"disambiguationData":[TD([[subQ2,-1.0]])],"derivedFrom":subQ1}),1.0]])]});}
            var Q10;
            {var subQ0=sQuery(id+"F14.wireOp",EDGE,"E71.MirrorCS");var subQ1=sQuery(id+"F14.wireOp",EDGE,"E66");var subQ2=makeQuery(id+"F14.imprint","INTERSECT",VERTEX,{"derivedFrom":[subQ1,subQ0]});Q10=makeQuery(id+"F14.imprint","IMPRINT",FACE,{"disambiguationData":[TD([[makeQuery(id+"F14.imprint","IMPRINT",EDGE,{"disambiguationData":[TD([[subQ2,1.0]])],"derivedFrom":subQ1}),1.0]])]});}
            var Q11;
            {var subQ0=sQuery(id+"F14.wireOp",EDGE,"E71.MirrorCS");var subQ1=sQuery(id+"F0.wireOp",EDGE,"E21");var subQ2=makeQuery(id+"F4.opRevolve","SWEPT_EDGE",EDGE,{"disambiguationData":[OSD([sQuery(id+"F0.wireOp",EDGE,"E20"),subQ1])]});var subQ3=makeQuery(id+"F14.imprint","INTERSECT",VERTEX,{"derivedFrom":[subQ2,subQ0]});Q11=makeQuery(id+"F14.imprint","IMPRINT",FACE,{"disambiguationData":[TD([[makeQuery(id+"F14.imprint","IMPRINT",EDGE,{"disambiguationData":[TD([[subQ3,-1.0]])],"derivedFrom":subQ0}),-1.0]])]});}
            var Q12;
            {var subQ0=sQuery(id+"F14.wireOp",EDGE,"E72.MirrorCS");var subQ1=sQuery(id+"F14.wireOp",EDGE,"E66");var subQ2=makeQuery(id+"F14.imprint","INTERSECT",VERTEX,{"derivedFrom":[subQ1,subQ0]});Q12=makeQuery(id+"F14.imprint","IMPRINT",FACE,{"disambiguationData":[TD([[makeQuery(id+"F14.imprint","IMPRINT",EDGE,{"disambiguationData":[TD([[subQ2,-1.0]])],"derivedFrom":subQ1}),1.0]])]});}
            var Q13;
            {var subQ0=sQuery(id+"F14.wireOp",EDGE,"E72.MirrorCS");var subQ1=sQuery(id+"F0.wireOp",EDGE,"E21");var subQ2=makeQuery(id+"F4.opRevolve","SWEPT_EDGE",EDGE,{"disambiguationData":[OSD([sQuery(id+"F0.wireOp",EDGE,"E20"),subQ1])]});var subQ3=makeQuery(id+"F14.imprint","INTERSECT",VERTEX,{"derivedFrom":[subQ2,subQ0]});Q13=makeQuery(id+"F14.imprint","IMPRINT",FACE,{"disambiguationData":[TD([[makeQuery(id+"F14.imprint","IMPRINT",EDGE,{"disambiguationData":[TD([[subQ3,-1.0]])],"derivedFrom":subQ0}),1.0]])]});}
            var Q14;
            {var subQ0=sQuery(id+"F14.wireOp",EDGE,"E78.MirrorCS");var subQ1=sQuery(id+"F14.wireOp",EDGE,"E66");var subQ2=makeQuery(id+"F14.imprint","INTERSECT",VERTEX,{"derivedFrom":[subQ1,subQ0]});Q14=makeQuery(id+"F14.imprint","IMPRINT",FACE,{"disambiguationData":[TD([[makeQuery(id+"F14.imprint","IMPRINT",EDGE,{"disambiguationData":[TD([[subQ2,1.0]])],"derivedFrom":subQ1}),1.0]])]});}
            var Q15;
            {var subQ0=sQuery(id+"F14.wireOp",EDGE,"E74.MirrorCS");var subQ1=sQuery(id+"F14.wireOp",EDGE,"E66");var subQ2=makeQuery(id+"F14.imprint","INTERSECT",VERTEX,{"derivedFrom":[subQ1,subQ0]});Q15=makeQuery(id+"F14.imprint","IMPRINT",FACE,{"disambiguationData":[TD([[makeQuery(id+"F14.imprint","IMPRINT",EDGE,{"disambiguationData":[TD([[subQ2,1.0]])],"derivedFrom":subQ1}),1.0]])]});}
            var Q16;
            {var subQ0=sQuery(id+"F14.wireOp",EDGE,"E74.MirrorCS");var subQ1=sQuery(id+"F0.wireOp",EDGE,"E21");var subQ2=makeQuery(id+"F4.opRevolve","SWEPT_EDGE",EDGE,{"disambiguationData":[OSD([sQuery(id+"F0.wireOp",EDGE,"E20"),subQ1])]});var subQ3=makeQuery(id+"F14.imprint","INTERSECT",VERTEX,{"derivedFrom":[subQ2,subQ0]});Q16=makeQuery(id+"F14.imprint","IMPRINT",FACE,{"disambiguationData":[TD([[makeQuery(id+"F14.imprint","IMPRINT",EDGE,{"disambiguationData":[TD([[subQ3,-1.0]])],"derivedFrom":subQ0}),-1.0]])]});}
            var Q17;
            {var subQ0=sQuery(id+"F14.wireOp",EDGE,"E73.MirrorCS");var subQ1=sQuery(id+"F14.wireOp",EDGE,"E66");var subQ2=makeQuery(id+"F14.imprint","INTERSECT",VERTEX,{"derivedFrom":[subQ1,subQ0]});Q17=makeQuery(id+"F14.imprint","IMPRINT",FACE,{"disambiguationData":[TD([[makeQuery(id+"F14.imprint","IMPRINT",EDGE,{"disambiguationData":[TD([[subQ2,-1.0]])],"derivedFrom":subQ1}),1.0]])]});}
            var Q18;
            {var subQ0=sQuery(id+"F14.wireOp",EDGE,"E73.MirrorCS");var subQ1=sQuery(id+"F0.wireOp",EDGE,"E21");var subQ2=makeQuery(id+"F4.opRevolve","SWEPT_EDGE",EDGE,{"disambiguationData":[OSD([sQuery(id+"F0.wireOp",EDGE,"E20"),subQ1])]});var subQ3=makeQuery(id+"F14.imprint","INTERSECT",VERTEX,{"derivedFrom":[subQ2,subQ0]});Q18=makeQuery(id+"F14.imprint","IMPRINT",FACE,{"disambiguationData":[TD([[makeQuery(id+"F14.imprint","IMPRINT",EDGE,{"disambiguationData":[TD([[subQ3,-1.0]])],"derivedFrom":subQ0}),1.0]])]});}
            var Q19;
            {var subQ0=sQuery(id+"F14.wireOp",EDGE,"E77.MirrorCS");var subQ1=sQuery(id+"F14.wireOp",EDGE,"E66");var subQ2=makeQuery(id+"F14.imprint","INTERSECT",VERTEX,{"derivedFrom":[subQ1,subQ0]});Q19=makeQuery(id+"F14.imprint","IMPRINT",FACE,{"disambiguationData":[TD([[makeQuery(id+"F14.imprint","IMPRINT",EDGE,{"disambiguationData":[TD([[subQ2,-1.0]])],"derivedFrom":subQ1}),1.0]])]});}
            var Q20;
            Q20=makeQuery(id+"F4.opRevolve","SWEPT_FACE",FACE,{"disambiguationData":[OSD([sQuery(id+"F0.wireOp",EDGE,"E23")])]});
            extrude(context, id + "F30", {"entities" : qUnion([Q0, Q1, Q2, Q3, Q4, Q5, Q6, Q7, Q8, Q9, Q10, Q11, Q12, Q13, Q14, Q15, Q16, Q17, Q18, Q19]), "operationType" : NewBodyOperationType.REMOVE, "endBound" : BoundingType.UP_TO_SURFACE, "oppositeDirection" : true, "depth" : 25.4 * mm, "endBoundEntityFace" : qUnion([Q20]), "offsetDistance" : 25.4 * mm});
        }
        {
            var Q0;
            {var subQ0=sQuery(id+"F16.wireOp",EDGE,"E95.0");var subQ1=sQuery(id+"F16.wireOp",EDGE,"E91.2.5.0");var subQ2=makeQuery(id+"F16.imprint","INTERSECT",VERTEX,{"derivedFrom":[subQ1,subQ0]});Q0=makeQuery(id+"F16.imprint","IMPRINT",FACE,{"disambiguationData":[TD([[makeQuery(id+"F16.imprint","IMPRINT",EDGE,{"disambiguationData":[TD([[subQ2,1.0]])],"derivedFrom":subQ1}),-1.0]])]});}
            var Q1;
            {var subQ0=sQuery(id+"F16.wireOp",EDGE,"E95.0");var subQ1=sQuery(id+"F16.wireOp",EDGE,"E91.2.4.0");var subQ2=makeQuery(id+"F16.imprint","INTERSECT",VERTEX,{"derivedFrom":[subQ1,subQ0]});Q1=makeQuery(id+"F16.imprint","IMPRINT",FACE,{"disambiguationData":[TD([[makeQuery(id+"F16.imprint","IMPRINT",EDGE,{"disambiguationData":[TD([[subQ2,1.0]])],"derivedFrom":subQ1}),-1.0]])]});}
            var Q2;
            {var subQ0=sQuery(id+"F16.wireOp",EDGE,"E95.0");var subQ1=sQuery(id+"F16.wireOp",EDGE,"E90.3.0");var subQ2=makeQuery(id+"F16.imprint","INTERSECT",VERTEX,{"derivedFrom":[subQ1,subQ0]});Q2=makeQuery(id+"F16.imprint","IMPRINT",FACE,{"disambiguationData":[TD([[makeQuery(id+"F16.imprint","IMPRINT",EDGE,{"disambiguationData":[TD([[subQ2,1.0]])],"derivedFrom":subQ1}),-1.0]])]});}
            var Q3;
            {var subQ0=sQuery(id+"F16.wireOp",EDGE,"E95.0");var subQ1=sQuery(id+"F16.wireOp",EDGE,"E90.2.0");var subQ2=makeQuery(id+"F16.imprint","INTERSECT",VERTEX,{"derivedFrom":[subQ1,subQ0]});Q3=makeQuery(id+"F16.imprint","IMPRINT",FACE,{"disambiguationData":[TD([[makeQuery(id+"F16.imprint","IMPRINT",EDGE,{"disambiguationData":[TD([[subQ2,1.0]])],"derivedFrom":subQ1}),-1.0]])]});}
            var Q4;
            {var subQ0=sQuery(id+"F16.wireOp",EDGE,"E95.0");var subQ1=sQuery(id+"F16.wireOp",EDGE,"E90.1.0");var subQ2=makeQuery(id+"F16.imprint","INTERSECT",VERTEX,{"derivedFrom":[subQ1,subQ0]});Q4=makeQuery(id+"F16.imprint","IMPRINT",FACE,{"disambiguationData":[TD([[makeQuery(id+"F16.imprint","IMPRINT",EDGE,{"disambiguationData":[TD([[subQ2,1.0]])],"derivedFrom":subQ1}),-1.0]])]});}
            var Q5;
            {var subQ0=sQuery(id+"F16.wireOp",EDGE,"E95.0");var subQ1=sQuery(id+"F16.wireOp",EDGE,"E87");var subQ2=makeQuery(id+"F16.imprint","INTERSECT",VERTEX,{"derivedFrom":[subQ1,subQ0]});Q5=makeQuery(id+"F16.imprint","IMPRINT",FACE,{"disambiguationData":[TD([[makeQuery(id+"F16.imprint","IMPRINT",EDGE,{"disambiguationData":[TD([[subQ2,-1.0]])],"derivedFrom":subQ1}),-1.0]])]});}
            extrude(context, id + "F31", {"entities" : qUnion([Q0, Q1, Q2, Q3, Q4, Q5]), "operationType" : NewBodyOperationType.REMOVE, "depth" : 25.4 * mm, "offsetDistance" : 25.4 * mm});
        }
        {
            var Q0;
            Q0=makeQuery(id+"F16.imprint","IMPRINT",FACE,{"disambiguationData":[TD([[makeQuery(id+"F16.imprint","IMPRINT",EDGE,{"derivedFrom":sQuery(id+"F16.wireOp",EDGE,"E97")}),1.0]])]});
            var Q1;
            Q1=makeQuery(id+"F16.imprint","IMPRINT",FACE,{"disambiguationData":[TD([[makeQuery(id+"F16.imprint","IMPRINT",EDGE,{"derivedFrom":sQuery(id+"F16.wireOp",EDGE,"E96")}),1.0]])]});
            extrude(context, id + "F32", {"entities" : qUnion([Q0, Q1]), "operationType" : NewBodyOperationType.REMOVE, "depth" : 25.4 * mm, "offsetDistance" : 25.4 * mm});
        }
        {
            var Q0;
            Q0=makeQuery(id+"F16.imprint","IMPRINT",FACE,{"disambiguationData":[TD([[makeQuery(id+"F16.imprint","IMPRINT",EDGE,{"derivedFrom":sQuery(id+"F16.wireOp",EDGE,"E97")}),1.0]])]});
            var Q1;
            Q1=makeQuery(id+"F12.opExtrude","CAP_FACE",FACE,{"disambiguationData":[OSD([sQuery(id+"F11.wireOp",EDGE,"E58.0"),sQuery(id+"F11.wireOp",EDGE,"E59"),sQuery(id+"F11.wireOp",EDGE,"E60.1.0"),sQuery(id+"F11.wireOp",EDGE,"E60.2.0"),sQuery(id+"F11.wireOp",EDGE,"E60.3.0"),sQuery(id+"F11.wireOp",EDGE,"E60.4.0"),sQuery(id+"F11.wireOp",EDGE,"E60.5.0")])],"isStart":true});
            var Q2;
            {var subQ0=sQuery(id+"F28.wireOp",EDGE,"E110.0.0");Q2=makeQuery(id+"F29.boolean.opBoolean","MERGE",FACE,{"derivedFrom":[makeQuery(id+"F10.opRevolve","SWEPT_FACE",FACE,{"disambiguationData":[OSD([sQuery(id+"F0.wireOp",EDGE,"E40")])]}),makeQuery(id+"F29.opExtrude","CAP_FACE",FACE,{"disambiguationData":[OSD([subQ0,sQuery(id+"F28.wireOp",EDGE,"E113.9.1")])],"isStart":false}),makeQuery(id+"F29.opExtrude","CAP_FACE",FACE,{"disambiguationData":[OSD([subQ0,sQuery(id+"F28.wireOp",EDGE,"E113.8.1")])],"isStart":false}),makeQuery(id+"F29.opExtrude","CAP_FACE",FACE,{"disambiguationData":[OSD([subQ0,sQuery(id+"F28.wireOp",EDGE,"E113.7.1")])],"isStart":false}),makeQuery(id+"F29.opExtrude","CAP_FACE",FACE,{"disambiguationData":[OSD([subQ0,sQuery(id+"F28.wireOp",EDGE,"E113.6.1")])],"isStart":false}),makeQuery(id+"F29.opExtrude","CAP_FACE",FACE,{"disambiguationData":[OSD([subQ0,sQuery(id+"F28.wireOp",EDGE,"E113.5.1")])],"isStart":false}),makeQuery(id+"F29.opExtrude","CAP_FACE",FACE,{"disambiguationData":[OSD([subQ0,sQuery(id+"F28.wireOp",EDGE,"E113.4.1")])],"isStart":false}),makeQuery(id+"F29.opExtrude","CAP_FACE",FACE,{"disambiguationData":[OSD([subQ0,sQuery(id+"F28.wireOp",EDGE,"E113.3.1")])],"isStart":false}),makeQuery(id+"F29.opExtrude","CAP_FACE",FACE,{"disambiguationData":[OSD([subQ0,sQuery(id+"F28.wireOp",EDGE,"E113.2.1")])],"isStart":false}),makeQuery(id+"F29.opExtrude","CAP_FACE",FACE,{"disambiguationData":[OSD([subQ0,sQuery(id+"F28.wireOp",EDGE,"E113.1.1")])],"isStart":false}),makeQuery(id+"F29.opExtrude","CAP_FACE",FACE,{"disambiguationData":[OSD([subQ0,sQuery(id+"F28.wireOp",EDGE,"E112")])],"isStart":false})]});}
            extrude(context, id + "F33", {"entities" : qUnion([Q0]), "operationType" : NewBodyOperationType.ADD, "endBound" : BoundingType.UP_TO_SURFACE, "depth" : 25.4 * mm, "endBoundEntityFace" : qUnion([Q1]), "offsetDistance" : 25.4 * mm, "hasSecondDirection" : true, "secondDirectionBound" : SecondDirectionBoundingType.UP_TO_SURFACE, "secondDirectionOppositeDirection" : false, "secondDirectionDepth" : 25.4 * mm, "secondDirectionBoundEntityFace" : qUnion([Q2])});
        }
        {
            var Q0;
            Q0=makeQuery(id+"F11.imprint","IMPRINT",FACE,{"disambiguationData":[TD([[makeQuery(id+"F11.imprint","IMPRINT",EDGE,{"derivedFrom":sQuery(id+"F11.wireOp",EDGE,"E60.3.0")}),1.0]])]});
            var Q1;
            Q1=makeQuery(id+"F11.imprint","IMPRINT",FACE,{"disambiguationData":[TD([[makeQuery(id+"F11.imprint","IMPRINT",EDGE,{"derivedFrom":sQuery(id+"F11.wireOp",EDGE,"E60.2.0")}),1.0]])]});
            var Q2;
            Q2=makeQuery(id+"F11.imprint","IMPRINT",FACE,{"disambiguationData":[TD([[makeQuery(id+"F11.imprint","IMPRINT",EDGE,{"derivedFrom":sQuery(id+"F11.wireOp",EDGE,"E60.1.0")}),1.0]])]});
            var Q3;
            Q3=makeQuery(id+"F11.imprint","IMPRINT",FACE,{"disambiguationData":[TD([[makeQuery(id+"F11.imprint","IMPRINT",EDGE,{"derivedFrom":sQuery(id+"F11.wireOp",EDGE,"E59")}),1.0]])]});
            var Q4;
            Q4=makeQuery(id+"F11.imprint","IMPRINT",FACE,{"disambiguationData":[TD([[makeQuery(id+"F11.imprint","IMPRINT",EDGE,{"derivedFrom":sQuery(id+"F11.wireOp",EDGE,"E60.5.0")}),1.0]])]});
            var Q5;
            Q5=makeQuery(id+"F11.imprint","IMPRINT",FACE,{"disambiguationData":[TD([[makeQuery(id+"F11.imprint","IMPRINT",EDGE,{"derivedFrom":sQuery(id+"F11.wireOp",EDGE,"E60.4.0")}),1.0]])]});
            extrude(context, id + "F34", {"entities" : qUnion([Q0, Q1, Q2, Q3, Q4, Q5]), "operationType" : NewBodyOperationType.REMOVE, "endBound" : BoundingType.THROUGH_ALL, "oppositeDirection" : true, "depth" : 25.4 * mm, "offsetDistance" : 25.4 * mm});
        }
        {
            var Q0;
            {var subQ0=sQuery(id+"F28.wireOp",EDGE,"E110.0.0");Q0=makeQuery(id+"F29.boolean.opBoolean","MERGE",FACE,{"derivedFrom":[makeQuery(id+"F12.opExtrude","CAP_FACE",FACE,{"disambiguationData":[OSD([sQuery(id+"F11.wireOp",EDGE,"E58.0"),sQuery(id+"F11.wireOp",EDGE,"E59"),sQuery(id+"F11.wireOp",EDGE,"E60.1.0"),sQuery(id+"F11.wireOp",EDGE,"E60.2.0"),sQuery(id+"F11.wireOp",EDGE,"E60.3.0"),sQuery(id+"F11.wireOp",EDGE,"E60.4.0"),sQuery(id+"F11.wireOp",EDGE,"E60.5.0")])],"isStart":false}),makeQuery(id+"F29.opExtrude","CAP_FACE",FACE,{"disambiguationData":[OSD([subQ0,sQuery(id+"F28.wireOp",EDGE,"E113.9.1")])],"isStart":true}),makeQuery(id+"F29.opExtrude","CAP_FACE",FACE,{"disambiguationData":[OSD([subQ0,sQuery(id+"F28.wireOp",EDGE,"E113.8.1")])],"isStart":true}),makeQuery(id+"F29.opExtrude","CAP_FACE",FACE,{"disambiguationData":[OSD([subQ0,sQuery(id+"F28.wireOp",EDGE,"E113.7.1")])],"isStart":true}),makeQuery(id+"F29.opExtrude","CAP_FACE",FACE,{"disambiguationData":[OSD([subQ0,sQuery(id+"F28.wireOp",EDGE,"E113.6.1")])],"isStart":true}),makeQuery(id+"F29.opExtrude","CAP_FACE",FACE,{"disambiguationData":[OSD([subQ0,sQuery(id+"F28.wireOp",EDGE,"E113.5.1")])],"isStart":true}),makeQuery(id+"F29.opExtrude","CAP_FACE",FACE,{"disambiguationData":[OSD([subQ0,sQuery(id+"F28.wireOp",EDGE,"E113.4.1")])],"isStart":true}),makeQuery(id+"F29.opExtrude","CAP_FACE",FACE,{"disambiguationData":[OSD([subQ0,sQuery(id+"F28.wireOp",EDGE,"E113.3.1")])],"isStart":true}),makeQuery(id+"F29.opExtrude","CAP_FACE",FACE,{"disambiguationData":[OSD([subQ0,sQuery(id+"F28.wireOp",EDGE,"E113.2.1")])],"isStart":true}),makeQuery(id+"F29.opExtrude","CAP_FACE",FACE,{"disambiguationData":[OSD([subQ0,sQuery(id+"F28.wireOp",EDGE,"E113.1.1")])],"isStart":true}),makeQuery(id+"F29.opExtrude","CAP_FACE",FACE,{"disambiguationData":[OSD([subQ0,sQuery(id+"F28.wireOp",EDGE,"E112")])],"isStart":true})]});}
            var sketch = newSketch(context, id + "F35", { "sketchPlane" : qUnion([Q0])});
            skLineSegment(sketch, "E114", {"start": v(0, 0) * mm, "end": v(-72.46, 0) * mm, "construction": true});
            skLineSegment(sketch, "E115.bottom", {"start": v(-17.78, 1.9) * mm, "end": v(-10.16, 1.9) * mm});
            skLineSegment(sketch, "E115.top", {"start": v(-17.78, -1.9) * mm, "end": v(-10.16, -1.9) * mm});
            skLineSegment(sketch, "E115.left", {"start": v(-17.78, 1.9) * mm, "end": v(-17.78, -1.9) * mm});
            skLineSegment(sketch, "E115.right", {"start": v(-10.16, 1.9) * mm, "end": v(-10.16, -1.9) * mm});
            skArc(sketch, "E116.0", {"start": v(-12.05, -4.02) * mm, "mid": v(-12.7, 0) * mm, "end": v(-12.05, 4.02) * mm});
            skSolve(sketch);
        }
        {
            var Q0;
            {var subQ0=sQuery(id+"F35.wireOp",EDGE,"E115.left");Q0=makeQuery(id+"F35.imprint","IMPRINT",FACE,{"disambiguationData":[TD([[makeQuery(id+"F35.imprint","IMPRINT",EDGE,{"derivedFrom":subQ0}),1.0]])]});}
            extrude(context, id + "F36", {"entities" : qUnion([Q0]), "operationType" : NewBodyOperationType.REMOVE, "endBound" : BoundingType.THROUGH_ALL, "oppositeDirection" : true, "depth" : 25.4 * mm, "offsetDistance" : 25.4 * mm});
        }
        {
            var Q0;
            {var subQ0=sQuery(id+"F26.wireOp",EDGE,"E104.0");Q0=makeQuery(id+"F27.boolean.opBoolean","MERGE",FACE,{"derivedFrom":[makeQuery(id+"F22.boolean.opBoolean","MERGE",FACE,{"derivedFrom":[makeQuery(id+"F9.opRevolve","SWEPT_FACE",FACE,{"disambiguationData":[OSD([sQuery(id+"F0.wireOp",EDGE,"E9"),sQuery(id+"F0.wireOp",EDGE,"E39")])]}),makeQuery(id+"F22.opExtrude","CAP_FACE",FACE,{"disambiguationData":[OSD([sQuery(id+"F16.wireOp",EDGE,"E93")])],"isStart":false})]}),makeQuery(id+"F27.opExtrude","CAP_FACE",FACE,{"disambiguationData":[OSD([subQ0,sQuery(id+"F26.wireOp",EDGE,"E109.5.0"),sQuery(id+"F26.wireOp",EDGE,"E109.5.1"),sQuery(id+"F26.wireOp",EDGE,"E109.5.2")])],"isStart":true}),makeQuery(id+"F27.opExtrude","CAP_FACE",FACE,{"disambiguationData":[OSD([subQ0,sQuery(id+"F26.wireOp",EDGE,"E109.4.0"),sQuery(id+"F26.wireOp",EDGE,"E109.4.1"),sQuery(id+"F26.wireOp",EDGE,"E109.4.2")])],"isStart":true}),makeQuery(id+"F27.opExtrude","CAP_FACE",FACE,{"disambiguationData":[OSD([subQ0,sQuery(id+"F26.wireOp",EDGE,"E109.3.0"),sQuery(id+"F26.wireOp",EDGE,"E109.3.1"),sQuery(id+"F26.wireOp",EDGE,"E109.3.2")])],"isStart":true}),makeQuery(id+"F27.opExtrude","CAP_FACE",FACE,{"disambiguationData":[OSD([subQ0,sQuery(id+"F26.wireOp",EDGE,"E109.2.0"),sQuery(id+"F26.wireOp",EDGE,"E109.2.1"),sQuery(id+"F26.wireOp",EDGE,"E109.2.2")])],"isStart":true}),makeQuery(id+"F27.opExtrude","CAP_FACE",FACE,{"disambiguationData":[OSD([subQ0,sQuery(id+"F26.wireOp",EDGE,"E109.1.0"),sQuery(id+"F26.wireOp",EDGE,"E109.1.1"),sQuery(id+"F26.wireOp",EDGE,"E109.1.2")])],"isStart":true}),makeQuery(id+"F27.opExtrude","CAP_FACE",FACE,{"disambiguationData":[OSD([subQ0,sQuery(id+"F26.wireOp",EDGE,"E106"),sQuery(id+"F26.wireOp",EDGE,"E107.MirrorCS"),sQuery(id+"F26.wireOp",EDGE,"E108")])],"isStart":true})]});}
            var sketch = newSketch(context, id + "F37", { "sketchPlane" : qUnion([Q0])});
            skLineSegment(sketch, "E117", {"start": v(0, 0) * mm, "end": v(-40.62, 0) * mm, "construction": true});
            skCircle(sketch, "E118", {"center": v(-20.08, 0) * mm, "radius": 1.27 * mm});
            skSolve(sketch);
        }
        {
            var Q0;
            {var subQ0=sQuery(id+"F37.wireOp",EDGE,"E118");var subQ1=makeQuery(id+"F9.opRevolve","SWEPT_EDGE",EDGE,{"disambiguationData":[OSD([sQuery(id+"F0.wireOp",EDGE,"E9"),sQuery(id+"F0.wireOp",EDGE,"E32"),sQuery(id+"F0.wireOp",EDGE,"E52")])]});var subQ2=makeQuery(id+"F37.imprint","INTERSECT",VERTEX,{"disambiguationData":[OD(0.0)],"derivedFrom":[subQ1,subQ0]});Q0=makeQuery(id+"F37.imprint","IMPRINT",FACE,{"disambiguationData":[TD([[makeQuery(id+"F37.imprint","IMPRINT",EDGE,{"disambiguationData":[TD([[subQ2,1.0]])],"derivedFrom":subQ0}),1.0]])]});}
            extrude(context, id + "F38", {"entities" : qUnion([Q0]), "operationType" : NewBodyOperationType.REMOVE, "endBound" : BoundingType.THROUGH_ALL, "oppositeDirection" : true, "depth" : 12.42 * mm, "offsetDistance" : 25.4 * mm});
        }
        {
            var Q0;
            {var subQ0=sQuery(id+"F24.wireOp",EDGE,"E98.0");Q0=makeQuery(id+"F25.boolean.opBoolean","MERGE",FACE,{"derivedFrom":[makeQuery(id+"F18.boolean.opBoolean","MERGE",FACE,{"derivedFrom":[makeQuery(id+"F8.opRevolve","SWEPT_FACE",FACE,{"disambiguationData":[OSD([sQuery(id+"F0.wireOp",EDGE,"E15"),sQuery(id+"F0.wireOp",EDGE,"E36")])]}),makeQuery(id+"F18.opExtrude","CAP_FACE",FACE,{"disambiguationData":[OSD([sQuery(id+"F16.wireOp",EDGE,"E83")])],"isStart":true})]}),makeQuery(id+"F25.opExtrude","CAP_FACE",FACE,{"disambiguationData":[OSD([subQ0,sQuery(id+"F24.wireOp",EDGE,"E103.7.0"),sQuery(id+"F24.wireOp",EDGE,"E103.7.2"),sQuery(id+"F24.wireOp",EDGE,"E103.7.3")])],"isStart":true}),makeQuery(id+"F25.opExtrude","CAP_FACE",FACE,{"disambiguationData":[OSD([subQ0,sQuery(id+"F24.wireOp",EDGE,"E103.6.0"),sQuery(id+"F24.wireOp",EDGE,"E103.6.2"),sQuery(id+"F24.wireOp",EDGE,"E103.6.3")])],"isStart":true}),makeQuery(id+"F25.opExtrude","CAP_FACE",FACE,{"disambiguationData":[OSD([subQ0,sQuery(id+"F24.wireOp",EDGE,"E103.5.0"),sQuery(id+"F24.wireOp",EDGE,"E103.5.2"),sQuery(id+"F24.wireOp",EDGE,"E103.5.3")])],"isStart":true}),makeQuery(id+"F25.opExtrude","CAP_FACE",FACE,{"disambiguationData":[OSD([subQ0,sQuery(id+"F24.wireOp",EDGE,"E103.4.0"),sQuery(id+"F24.wireOp",EDGE,"E103.4.2"),sQuery(id+"F24.wireOp",EDGE,"E103.4.3")])],"isStart":true}),makeQuery(id+"F25.opExtrude","CAP_FACE",FACE,{"disambiguationData":[OSD([subQ0,sQuery(id+"F24.wireOp",EDGE,"E103.3.0"),sQuery(id+"F24.wireOp",EDGE,"E103.3.2"),sQuery(id+"F24.wireOp",EDGE,"E103.3.3")])],"isStart":true}),makeQuery(id+"F25.opExtrude","CAP_FACE",FACE,{"disambiguationData":[OSD([subQ0,sQuery(id+"F24.wireOp",EDGE,"E103.2.0"),sQuery(id+"F24.wireOp",EDGE,"E103.2.2"),sQuery(id+"F24.wireOp",EDGE,"E103.2.3")])],"isStart":true}),makeQuery(id+"F25.opExtrude","CAP_FACE",FACE,{"disambiguationData":[OSD([subQ0,sQuery(id+"F24.wireOp",EDGE,"E103.1.0"),sQuery(id+"F24.wireOp",EDGE,"E103.1.2"),sQuery(id+"F24.wireOp",EDGE,"E103.1.3")])],"isStart":true}),makeQuery(id+"F25.opExtrude","CAP_FACE",FACE,{"disambiguationData":[OSD([subQ0,sQuery(id+"F24.wireOp",EDGE,"E100"),sQuery(id+"F24.wireOp",EDGE,"E101.MirrorCS"),sQuery(id+"F24.wireOp",EDGE,"E102")])],"isStart":true})]});}
            var sketch = newSketch(context, id + "F39", { "sketchPlane" : qUnion([Q0])});
            skLineSegment(sketch, "E119", {"start": v(0, 0) * mm, "end": v(-73.72, 0) * mm, "construction": true});
            skCircle(sketch, "E120", {"center": v(-24.65, 0) * mm, "radius": 1.27 * mm});
            skSolve(sketch);
        }
        {
            var Q0;
            {var subQ0=sQuery(id+"F39.wireOp",EDGE,"E120");var subQ1=makeQuery(id+"F8.opRevolve","SWEPT_EDGE",EDGE,{"disambiguationData":[OSD([sQuery(id+"F0.wireOp",EDGE,"E15"),sQuery(id+"F0.wireOp",EDGE,"E43")])]});var subQ2=makeQuery(id+"F39.imprint","INTERSECT",VERTEX,{"disambiguationData":[OD(0.0)],"derivedFrom":[subQ1,subQ0]});Q0=makeQuery(id+"F39.imprint","IMPRINT",FACE,{"disambiguationData":[TD([[makeQuery(id+"F39.imprint","IMPRINT",EDGE,{"disambiguationData":[TD([[subQ2,1.0]])],"derivedFrom":subQ0}),1.0]])]});}
            extrude(context, id + "F40", {"entities" : qUnion([Q0]), "operationType" : NewBodyOperationType.REMOVE, "endBound" : BoundingType.THROUGH_ALL, "oppositeDirection" : true, "depth" : 25.4 * mm, "offsetDistance" : 25.4 * mm});
        }
    });
